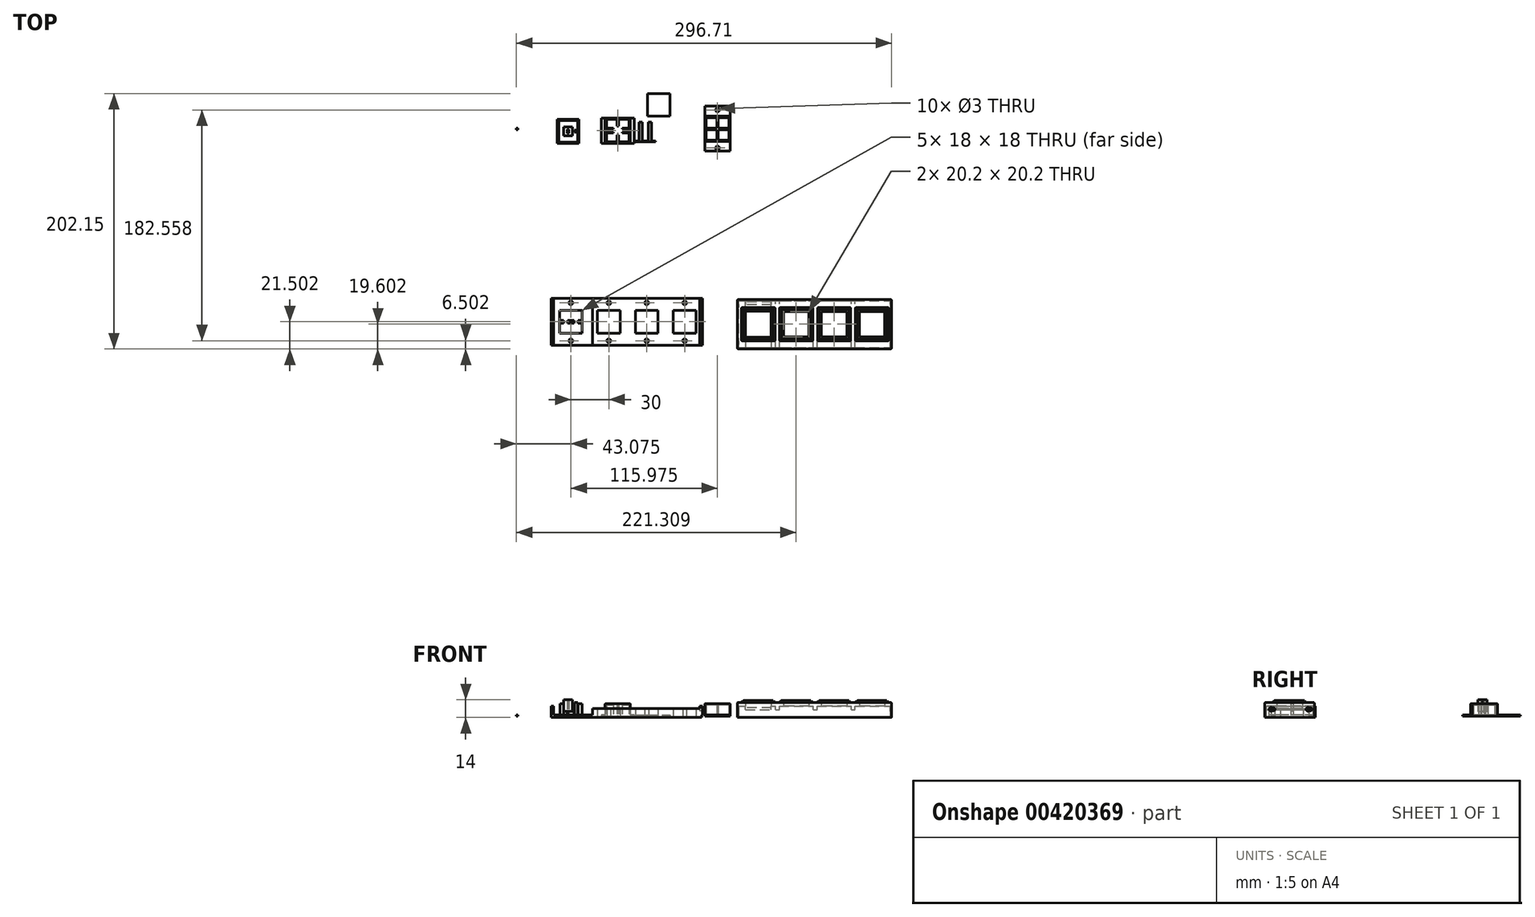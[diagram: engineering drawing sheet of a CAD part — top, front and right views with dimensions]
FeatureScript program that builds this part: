
annotation { "Feature Type Name" : "Feature", "Feature Type Description" : "" }
export const myFeature = defineFeature(function(context is Context, id is Id, definition is map)
    precondition{}
    {
        {
            var Q0;
            Q0=qCreatedBy(makeId("Top.planeOp"),FACE);
            var sketch = newSketch(context, id + "F0", { "sketchPlane" : qUnion([Q0])});
            skPoint(sketch, "E0.middle", {"position": v(0, 0) * mm});
            skLineSegment(sketch, "E1.bottom", {"start": v(10, -10) * mm, "end": v(-10, -10) * mm});
            skLineSegment(sketch, "E1.top", {"start": v(10, 10) * mm, "end": v(-10, 10) * mm});
            skLineSegment(sketch, "E1.left", {"start": v(10, -10) * mm, "end": v(10, 10) * mm});
            skLineSegment(sketch, "E1.right", {"start": v(-10, -10) * mm, "end": v(-10, 10) * mm});
            skSolve(sketch);
        }
        {
            var Q0;
            Q0=makeQuery(id+"F0.imprint","IMPRINT",FACE,{"disambiguationData":[TD([[makeQuery(id+"F0.imprint","IMPRINT",EDGE,{"derivedFrom":sQuery(id+"F0.wireOp",EDGE,"E1.bottom")}),-1.0]])]});
            extrude(context, id + "F1", {"entities" : qUnion([Q0]), "depth" : 10 * mm});
        }
        {
            var Q0;
            Q0=makeQuery(id+"F1.opExtrude","CAP_FACE",FACE,{"disambiguationData":[OSD([sQuery(id+"F0.wireOp",EDGE,"E1.bottom"),sQuery(id+"F0.wireOp",EDGE,"E1.top"),sQuery(id+"F0.wireOp",EDGE,"E1.left"),sQuery(id+"F0.wireOp",EDGE,"E1.right")])],"isStart":true});
            shell(context, id + "F2", {"entities" : qUnion([Q0]), "thickness" : 1 * mm});
        }
        {
            var Q0;
            Q0=qCreatedBy(makeId("Top.planeOp"),FACE);
            var sketch = newSketch(context, id + "F3", { "sketchPlane" : qUnion([Q0])});
            skLineSegment(sketch, "E2.bottom", {"start": v(0.5, -9) * mm, "end": v(-0.5, -9) * mm});
            skLineSegment(sketch, "E2.top", {"start": v(0.5, 9) * mm, "end": v(-0.5, 9) * mm});
            skLineSegment(sketch, "E2.left", {"start": v(0.5, -9) * mm, "end": v(0.5, -0.5) * mm});
            skLineSegment(sketch, "E2.right", {"start": v(-0.5, -9) * mm, "end": v(-0.5, -0.5) * mm});
            skLineSegment(sketch, "E3.bottom", {"start": v(9, 0.5) * mm, "end": v(0.5, 0.5) * mm});
            skLineSegment(sketch, "E3.top", {"start": v(9, -0.5) * mm, "end": v(0.5, -0.5) * mm});
            skLineSegment(sketch, "E3.left", {"start": v(9, 0.5) * mm, "end": v(9, -0.5) * mm});
            skLineSegment(sketch, "E3.right", {"start": v(-9, 0.5) * mm, "end": v(-9, -0.5) * mm});
            skLineSegment(sketch, "E4.trimOffspring", {"start": v(-0.5, 0.5) * mm, "end": v(-0.5, 9) * mm});
            skLineSegment(sketch, "E5.trimOffspring", {"start": v(-0.5, -0.5) * mm, "end": v(-9, -0.5) * mm});
            skLineSegment(sketch, "E6.trimOffspring", {"start": v(0.5, 0.5) * mm, "end": v(0.5, 9) * mm});
            skLineSegment(sketch, "E7.trimOffspring", {"start": v(-0.5, 0.5) * mm, "end": v(-9, 0.5) * mm});
            skSolve(sketch);
        }
        {
            var Q0;
            Q0=qSketchRegion(id+"F3",true);
            extrude(context, id + "F4", {"entities" : qUnion([Q0]), "operationType" : NewBodyOperationType.ADD, "depth" : 9 * mm});
        }
        {
            var Q0;
            Q0=qCreatedBy(makeId("Top.planeOp"),FACE);
            var sketch = newSketch(context, id + "F5", { "sketchPlane" : qUnion([Q0])});
            skLineSegment(sketch, "E8.bottom", {"start": v(-10, -9.5) * mm, "end": v(10, -9.5) * mm});
            skLineSegment(sketch, "E8.top", {"start": v(-10, -17.5) * mm, "end": v(10, -17.5) * mm});
            skLineSegment(sketch, "E8.left", {"start": v(-10, -9.5) * mm, "end": v(-10, -17.5) * mm});
            skLineSegment(sketch, "E8.right", {"start": v(10, -9.5) * mm, "end": v(10, -17.5) * mm});
            skLineSegment(sketch, "E9.bottom", {"start": v(-10, 10) * mm, "end": v(10, 10) * mm});
            skLineSegment(sketch, "E9.top", {"start": v(-10, 18) * mm, "end": v(10, 18) * mm});
            skLineSegment(sketch, "E9.left", {"start": v(-10, 10) * mm, "end": v(-10, 18) * mm});
            skLineSegment(sketch, "E9.right", {"start": v(10, 10) * mm, "end": v(10, 18) * mm});
            skLineSegment(sketch, "E10.bottom", {"start": v(-10, -9.5) * mm, "end": v(-13, -9.5) * mm, "construction": true});
            skLineSegment(sketch, "E10.top", {"start": v(-10, 10) * mm, "end": v(-13, 10) * mm, "construction": true});
            skLineSegment(sketch, "E10.left", {"start": v(-10, -9.5) * mm, "end": v(-10, 10) * mm});
            skLineSegment(sketch, "E10.right", {"start": v(-13, -9.5) * mm, "end": v(-13, 10) * mm, "construction": true});
            skLineSegment(sketch, "E11.bottom", {"start": v(10, -9.5) * mm, "end": v(13, -9.5) * mm, "construction": true});
            skLineSegment(sketch, "E11.top", {"start": v(10, 10) * mm, "end": v(13, 10) * mm, "construction": true});
            skLineSegment(sketch, "E11.left", {"start": v(10, -9.5) * mm, "end": v(10, 10) * mm});
            skLineSegment(sketch, "E11.right", {"start": v(13, -9.5) * mm, "end": v(13, 10) * mm, "construction": true});
            skCircle(sketch, "E12", {"center": v(0, 15) * mm, "radius": 1.5 * mm});
            skCircle(sketch, "E13", {"center": v(0, -15) * mm, "radius": 1.5 * mm});
            skSolve(sketch);
        }
        {
            var Q0;
            Q0=makeQuery(id+"F5.imprint","IMPRINT",FACE,{"disambiguationData":[TD([[makeQuery(id+"F5.imprint","IMPRINT",EDGE,{"derivedFrom":sQuery(id+"F5.wireOp",EDGE,"E10.bottom")}),-1.0]])]});
            var Q1;
            Q1=makeQuery(id+"F5.imprint","IMPRINT",FACE,{"disambiguationData":[TD([[makeQuery(id+"F5.imprint","IMPRINT",EDGE,{"derivedFrom":sQuery(id+"F5.wireOp",EDGE,"E8.bottom")}),-1.0]])]});
            var Q2;
            Q2=makeQuery(id+"F5.imprint","IMPRINT",FACE,{"disambiguationData":[TD([[makeQuery(id+"F5.imprint","IMPRINT",EDGE,{"derivedFrom":sQuery(id+"F5.wireOp",EDGE,"E11.bottom")}),1.0]])]});
            var Q3;
            Q3=makeQuery(id+"F5.imprint","IMPRINT",FACE,{"disambiguationData":[TD([[makeQuery(id+"F5.imprint","IMPRINT",EDGE,{"derivedFrom":sQuery(id+"F5.wireOp",EDGE,"E9.bottom")}),1.0]])]});
            extrude(context, id + "F6", {"entities" : qUnion([Q0, Q1, Q2, Q3]), "operationType" : NewBodyOperationType.ADD, "depth" : 1 * mm});
        }
        {
            var Q0;
            Q0=qCreatedBy(makeId("Top.planeOp"),FACE);
            var sketch = newSketch(context, id + "F7", { "sketchPlane" : qUnion([Q0])});
            skLineSegment(sketch, "E14.bottom", {"start": v(-88.88, 8.7) * mm, "end": v(-68.88, 8.7) * mm});
            skLineSegment(sketch, "E14.top", {"start": v(-88.88, -11.3) * mm, "end": v(-68.88, -11.3) * mm});
            skLineSegment(sketch, "E14.left", {"start": v(-88.88, 8.7) * mm, "end": v(-88.88, -11.3) * mm});
            skLineSegment(sketch, "E14.right", {"start": v(-68.88, 8.7) * mm, "end": v(-68.88, -11.3) * mm});
            skSolve(sketch);
        }
        {
            var Q0;
            Q0=makeQuery(id+"F7.imprint","IMPRINT",FACE,{"disambiguationData":[TD([[makeQuery(id+"F7.imprint","IMPRINT",EDGE,{"derivedFrom":sQuery(id+"F7.wireOp",EDGE,"E14.bottom")}),-1.0]])]});
            extrude(context, id + "F8", {"entities" : qUnion([Q0]), "depth" : 10 * mm});
        }
        {
            var Q0;
            Q0=makeQuery(id+"F13.boolean.opBoolean","MERGE",FACE,{"derivedFrom":[makeQuery(id+"F8.opExtrude","CAP_FACE",FACE,{"disambiguationData":[OSD([sQuery(id+"F7.wireOp",EDGE,"E14.bottom"),sQuery(id+"F7.wireOp",EDGE,"E14.top"),sQuery(id+"F7.wireOp",EDGE,"E14.left"),sQuery(id+"F7.wireOp",EDGE,"E14.right")])],"isStart":true}),makeQuery(id+"F13.opExtrude","CAP_FACE",FACE,{"disambiguationData":[OSD([sQuery(id+"F12.wireOp",EDGE,"E22.bottom"),sQuery(id+"F12.wireOp",EDGE,"E22.top"),sQuery(id+"F12.wireOp",EDGE,"E22.left"),sQuery(id+"F12.wireOp",EDGE,"E22.right"),sQuery(id+"F12.wireOp",EDGE,"E23.trimOffspring"),sQuery(id+"F12.wireOp",EDGE,"E25.trimOffspring"),sQuery(id+"F12.wireOp",EDGE,"E27"),sQuery(id+"F12.wireOp",EDGE,"E28"),sQuery(id+"F12.wireOp",EDGE,"E29.bottom"),sQuery(id+"F12.wireOp",EDGE,"E29.top"),sQuery(id+"F12.wireOp",EDGE,"E29.left"),sQuery(id+"F12.wireOp",EDGE,"E30.bottom"),sQuery(id+"F12.wireOp",EDGE,"E30.top"),sQuery(id+"F12.wireOp",EDGE,"E30.left"),sQuery(id+"F12.wireOp",EDGE,"E31.bottom"),sQuery(id+"F12.wireOp",EDGE,"E31.top"),sQuery(id+"F12.wireOp",EDGE,"E31.right"),sQuery(id+"F12.wireOp",EDGE,"E32.bottom"),sQuery(id+"F12.wireOp",EDGE,"E32.top"),sQuery(id+"F12.wireOp",EDGE,"E32.right")])],"isStart":true})]});
            var sketch = newSketch(context, id + "F9", { "sketchPlane" : qUnion([Q0])});
            skLineSegment(sketch, "E15.bottom", {"start": v(-88.88, 11.3) * mm, "end": v(-68.88, 11.3) * mm});
            skLineSegment(sketch, "E15.top", {"start": v(-88.88, 14.3) * mm, "end": v(-68.88, 14.3) * mm, "construction": true});
            skLineSegment(sketch, "E15.left", {"start": v(-88.88, 11.3) * mm, "end": v(-88.88, 14.3) * mm, "construction": true});
            skLineSegment(sketch, "E15.right", {"start": v(-68.88, 11.3) * mm, "end": v(-68.88, 14.3) * mm, "construction": true});
            skLineSegment(sketch, "E16.bottom", {"start": v(-88.88, -8.7) * mm, "end": v(-68.88, -8.7) * mm});
            skLineSegment(sketch, "E16.top", {"start": v(-88.88, -11.7) * mm, "end": v(-68.88, -11.7) * mm});
            skLineSegment(sketch, "E16.left", {"start": v(-88.88, -8.7) * mm, "end": v(-88.88, -11.7) * mm, "construction": true});
            skLineSegment(sketch, "E16.right", {"start": v(-68.88, -8.7) * mm, "end": v(-68.88, -11.7) * mm, "construction": true});
            skLineSegment(sketch, "E17.bottom", {"start": v(-88.88, -8.7) * mm, "end": v(-91.88, -8.7) * mm});
            skLineSegment(sketch, "E17.top", {"start": v(-88.88, 11.3) * mm, "end": v(-91.88, 11.3) * mm});
            skLineSegment(sketch, "E17.left", {"start": v(-88.88, -8.7) * mm, "end": v(-88.88, 11.3) * mm});
            skLineSegment(sketch, "E17.right", {"start": v(-91.88, -8.7) * mm, "end": v(-91.88, 11.3) * mm});
            skLineSegment(sketch, "E18.bottom", {"start": v(-68.88, -8.7) * mm, "end": v(-65.88, -8.7) * mm});
            skLineSegment(sketch, "E18.top", {"start": v(-68.88, 11.3) * mm, "end": v(-65.88, 11.3) * mm});
            skLineSegment(sketch, "E18.left", {"start": v(-68.88, -8.7) * mm, "end": v(-68.88, 11.3) * mm});
            skLineSegment(sketch, "E18.right", {"start": v(-65.88, -8.7) * mm, "end": v(-65.88, 11.3) * mm});
            skLineSegment(sketch, "E19.bottom", {"start": v(-88.88, -11.7) * mm, "end": v(-68.88, -11.7) * mm, "construction": true});
            skLineSegment(sketch, "E19.top", {"start": v(-88.88, -16.7) * mm, "end": v(-68.88, -16.7) * mm, "construction": true});
            skLineSegment(sketch, "E19.left", {"start": v(-88.88, -11.7) * mm, "end": v(-88.88, -16.7) * mm, "construction": true});
            skLineSegment(sketch, "E19.right", {"start": v(-68.88, -11.7) * mm, "end": v(-68.88, -16.7) * mm, "construction": true});
            skCircle(sketch, "E20", {"center": v(-78.88, -13.7) * mm, "radius": 1.5 * mm, "construction": true});
            skSolve(sketch);
        }
        {
            var Q0;
            Q0=qSketchRegion(id+"F9",true);
            extrude(context, id + "F10", {"entities" : qUnion([Q0]), "operationType" : NewBodyOperationType.ADD, "oppositeDirection" : true, "depth" : 0.95 * mm});
        }
        {
            var Q0;
            Q0=makeQuery(id+"F8.opExtrude","CAP_FACE",FACE,{"disambiguationData":[OSD([sQuery(id+"F7.wireOp",EDGE,"E14.bottom"),sQuery(id+"F7.wireOp",EDGE,"E14.top"),sQuery(id+"F7.wireOp",EDGE,"E14.left"),sQuery(id+"F7.wireOp",EDGE,"E14.right")])],"isStart":true});
            shell(context, id + "F11", {"entities" : qUnion([Q0]), "thickness" : 1 * mm});
        }
        {
            var Q0;
            Q0=qCreatedBy(makeId("Top.planeOp"),FACE);
            var sketch = newSketch(context, id + "F12", { "sketchPlane" : qUnion([Q0])});
            skLineSegment(sketch, "E21.bottom", {"start": v(-87.88, -0.1) * mm, "end": v(-79.38, -0.1) * mm, "construction": true});
            skLineSegment(sketch, "E21.top", {"start": v(-87.88, -2.5) * mm, "end": v(-79.38, -2.5) * mm, "construction": true});
            skLineSegment(sketch, "E21.left", {"start": v(-87.88, -0.1) * mm, "end": v(-87.88, -2.5) * mm, "construction": true});
            skLineSegment(sketch, "E21.right", {"start": v(-69.88, -0.1) * mm, "end": v(-69.88, -2.5) * mm, "construction": true});
            skLineSegment(sketch, "E22.bottom", {"start": v(-79.38, 7.7) * mm, "end": v(-78.38, 7.7) * mm});
            skLineSegment(sketch, "E22.top", {"start": v(-79.38, -10.3) * mm, "end": v(-78.38, -10.3) * mm});
            skLineSegment(sketch, "E22.left", {"start": v(-79.38, 7.7) * mm, "end": v(-79.38, -0.1) * mm});
            skLineSegment(sketch, "E22.right", {"start": v(-78.38, 7.7) * mm, "end": v(-78.38, -0.1) * mm});
            skLineSegment(sketch, "E23.trimOffspring", {"start": v(-79.38, -10.3) * mm, "end": v(-79.38, -2.5) * mm});
            skLineSegment(sketch, "E24.trimOffspring", {"start": v(-78.38, -0.1) * mm, "end": v(-69.88, -0.1) * mm, "construction": true});
            skLineSegment(sketch, "E25.trimOffspring", {"start": v(-78.38, -2.5) * mm, "end": v(-78.38, -10.3) * mm});
            skLineSegment(sketch, "E26.trimOffspring", {"start": v(-78.38, -2.5) * mm, "end": v(-69.88, -2.5) * mm, "construction": true});
            skLineSegment(sketch, "E27", {"start": v(-79.38, -2.5) * mm, "end": v(-79.38, -0.1) * mm});
            skLineSegment(sketch, "E28", {"start": v(-78.38, -2.5) * mm, "end": v(-78.38, -0.1) * mm});
            skLineSegment(sketch, "E29.bottom", {"start": v(-87.88, -2.5) * mm, "end": v(-79.38, -2.5) * mm});
            skLineSegment(sketch, "E29.top", {"start": v(-87.88, -3.3) * mm, "end": v(-79.38, -3.3) * mm});
            skLineSegment(sketch, "E29.left", {"start": v(-87.88, -2.5) * mm, "end": v(-87.88, -3.3) * mm});
            skLineSegment(sketch, "E29.right", {"start": v(-79.38, -2.5) * mm, "end": v(-79.38, -3.3) * mm});
            skLineSegment(sketch, "E30.bottom", {"start": v(-87.88, -0.1) * mm, "end": v(-79.38, -0.1) * mm});
            skLineSegment(sketch, "E30.top", {"start": v(-87.88, 0.7) * mm, "end": v(-79.38, 0.7) * mm});
            skLineSegment(sketch, "E30.left", {"start": v(-87.88, -0.1) * mm, "end": v(-87.88, 0.7) * mm});
            skLineSegment(sketch, "E30.right", {"start": v(-79.38, -0.1) * mm, "end": v(-79.38, 0.7) * mm});
            skLineSegment(sketch, "E31.bottom", {"start": v(-78.38, -3.3) * mm, "end": v(-69.88, -3.3) * mm});
            skLineSegment(sketch, "E31.top", {"start": v(-78.38, -2.5) * mm, "end": v(-69.88, -2.5) * mm});
            skLineSegment(sketch, "E31.left", {"start": v(-78.38, -3.3) * mm, "end": v(-78.38, -2.5) * mm});
            skLineSegment(sketch, "E31.right", {"start": v(-69.88, -3.3) * mm, "end": v(-69.88, -2.5) * mm});
            skLineSegment(sketch, "E32.bottom", {"start": v(-78.38, -0.1) * mm, "end": v(-69.88, -0.1) * mm});
            skLineSegment(sketch, "E32.top", {"start": v(-78.38, 0.7) * mm, "end": v(-69.88, 0.7) * mm});
            skLineSegment(sketch, "E32.left", {"start": v(-78.38, -0.1) * mm, "end": v(-78.38, 0.7) * mm});
            skLineSegment(sketch, "E32.right", {"start": v(-69.88, -0.1) * mm, "end": v(-69.88, 0.7) * mm});
            skSolve(sketch);
        }
        {
            var Q0;
            Q0=makeQuery(id+"F12.imprint","IMPRINT",FACE,{"disambiguationData":[TD([[makeQuery(id+"F12.imprint","IMPRINT",EDGE,{"derivedFrom":sQuery(id+"F12.wireOp",EDGE,"E22.bottom")}),-1.0]])]});
            var Q1;
            Q1=makeQuery(id+"F12.imprint","IMPRINT",FACE,{"disambiguationData":[TD([[makeQuery(id+"F12.imprint","IMPRINT",EDGE,{"derivedFrom":sQuery(id+"F12.wireOp",EDGE,"E29.bottom")}),-1.0]])]});
            var Q2;
            Q2=makeQuery(id+"F12.imprint","IMPRINT",FACE,{"disambiguationData":[TD([[makeQuery(id+"F12.imprint","IMPRINT",EDGE,{"derivedFrom":sQuery(id+"F12.wireOp",EDGE,"E30.bottom")}),1.0]])]});
            var Q3;
            Q3=makeQuery(id+"F12.imprint","IMPRINT",FACE,{"disambiguationData":[TD([[makeQuery(id+"F12.imprint","IMPRINT",EDGE,{"derivedFrom":sQuery(id+"F12.wireOp",EDGE,"E32.bottom")}),1.0]])]});
            var Q4;
            Q4=makeQuery(id+"F12.imprint","IMPRINT",FACE,{"disambiguationData":[TD([[makeQuery(id+"F12.imprint","IMPRINT",EDGE,{"derivedFrom":sQuery(id+"F12.wireOp",EDGE,"E31.bottom")}),1.0]])]});
            var Q5;
            Q5=sQuery(id+"F12.wireOp",EDGE,"E22.left");
            var Q6;
            Q6=sQuery(id+"F12.wireOp",EDGE,"E23.trimOffspring");
            var Q7;
            Q7=sQuery(id+"F12.wireOp",EDGE,"E21.top");
            var Q8;
            Q8=sQuery(id+"F12.wireOp",EDGE,"E24.trimOffspring");
            var Q9;
            Q9=sQuery(id+"F12.wireOp",EDGE,"E22.bottom");
            var Q10;
            Q10=sQuery(id+"F12.wireOp",EDGE,"E22.right");
            var Q11;
            Q11=sQuery(id+"F12.wireOp",EDGE,"E22.top");
            var Q12;
            Q12=sQuery(id+"F12.wireOp",EDGE,"E21.bottom");
            var Q13;
            Q13=sQuery(id+"F12.wireOp",EDGE,"E25.trimOffspring");
            var Q14;
            Q14=sQuery(id+"F12.wireOp",EDGE,"E26.trimOffspring");
            var Q15;
            Q15=sQuery(id+"F12.wireOp",EDGE,"E21.right");
            var Q16;
            Q16=sQuery(id+"F12.wireOp",EDGE,"E21.left");
            extrude(context, id + "F13", {"entities" : qUnion([Q0, Q1, Q2, Q3, Q4]), "operationType" : NewBodyOperationType.ADD, "surfaceEntities" : qUnion([Q5, Q6, Q7, Q8, Q9, Q10, Q11, Q12, Q13, Q14, Q15, Q16]), "depth" : 9 * mm});
        }
        {
            var Q0;
            Q0=makeQuery(id+"F13.boolean.opBoolean","MERGE",FACE,{"derivedFrom":[makeQuery(id+"F8.opExtrude","CAP_FACE",FACE,{"disambiguationData":[OSD([sQuery(id+"F7.wireOp",EDGE,"E14.bottom"),sQuery(id+"F7.wireOp",EDGE,"E14.top"),sQuery(id+"F7.wireOp",EDGE,"E14.left"),sQuery(id+"F7.wireOp",EDGE,"E14.right")])],"isStart":true}),makeQuery(id+"F13.opExtrude","CAP_FACE",FACE,{"disambiguationData":[OSD([sQuery(id+"F12.wireOp",EDGE,"E21.bottom"),sQuery(id+"F12.wireOp",EDGE,"E21.top"),sQuery(id+"F12.wireOp",EDGE,"E21.left"),sQuery(id+"F12.wireOp",EDGE,"E21.right"),sQuery(id+"F12.wireOp",EDGE,"E22.bottom"),sQuery(id+"F12.wireOp",EDGE,"E22.top"),sQuery(id+"F12.wireOp",EDGE,"E22.left"),sQuery(id+"F12.wireOp",EDGE,"E22.right"),sQuery(id+"F12.wireOp",EDGE,"E23.trimOffspring"),sQuery(id+"F12.wireOp",EDGE,"E24.trimOffspring"),sQuery(id+"F12.wireOp",EDGE,"E25.trimOffspring"),sQuery(id+"F12.wireOp",EDGE,"E26.trimOffspring")])],"isStart":true})]});
            var sketch = newSketch(context, id + "F14", { "sketchPlane" : qUnion([Q0])});
            skLineSegment(sketch, "E33.bottom", {"start": v(-75.28, -2.3) * mm, "end": v(-82.48, -2.3) * mm});
            skLineSegment(sketch, "E33.top", {"start": v(-75.28, 4.9) * mm, "end": v(-82.48, 4.9) * mm});
            skLineSegment(sketch, "E33.left", {"start": v(-75.28, -2.3) * mm, "end": v(-75.28, 4.9) * mm});
            skLineSegment(sketch, "E33.right", {"start": v(-82.48, -2.3) * mm, "end": v(-82.48, 4.9) * mm});
            skPoint(sketch, "E33.middle.positionSnap1", {"position": v(-88.88, 1.8) * mm});
            skSolve(sketch);
        }
        {
            var Q0;
            {var subQ1=makeQuery(id+"F13.opExtrude","CAP_EDGE",EDGE,{"disambiguationData":[OSD([sQuery(id+"F12.wireOp",EDGE,"E22.right")])],"isStart":true});var subQ3=sQuery(id+"F14.wireOp",EDGE,"E33.bottom");var subQ4=makeQuery(id+"F14.imprint","INTERSECT",VERTEX,{"derivedFrom":[subQ1,subQ3]});Q0=makeQuery(id+"F14.imprint","IMPRINT",FACE,{"disambiguationData":[TD([[makeQuery(id+"F14.imprint","IMPRINT",EDGE,{"disambiguationData":[TD([[subQ4,-1.0]])],"derivedFrom":subQ3}),-1.0]])]});}
            extrude(context, id + "F15", {"entities" : qUnion([Q0]), "operationType" : NewBodyOperationType.REMOVE, "oppositeDirection" : true, "depth" : 9 * mm});
        }
        {
            var Q0;
            Q0=qCreatedBy(makeId("Top.planeOp"),FACE);
            var sketch = newSketch(context, id + "F16", { "sketchPlane" : qUnion([Q0])});
            skLineSegment(sketch, "E34.bottom", {"start": v(-126.7, 7.66) * mm, "end": v(-109.7, 7.66) * mm});
            skLineSegment(sketch, "E34.top", {"start": v(-126.7, -11.34) * mm, "end": v(-109.7, -11.34) * mm});
            skLineSegment(sketch, "E34.left", {"start": v(-126.7, 7.66) * mm, "end": v(-126.7, -11.34) * mm});
            skLineSegment(sketch, "E34.right", {"start": v(-109.7, 7.66) * mm, "end": v(-109.7, -11.34) * mm});
            skLineSegment(sketch, "E35.top", {"start": v(-126.7, 15.66) * mm, "end": v(-109.7, 15.66) * mm});
            skLineSegment(sketch, "E35.left", {"start": v(-126.7, 7.66) * mm, "end": v(-126.7, 15.66) * mm});
            skLineSegment(sketch, "E35.right", {"start": v(-109.7, 7.66) * mm, "end": v(-109.7, 15.66) * mm});
            skLineSegment(sketch, "E36.top", {"start": v(-126.7, -19.34) * mm, "end": v(-109.7, -19.34) * mm});
            skLineSegment(sketch, "E36.left", {"start": v(-126.7, -11.34) * mm, "end": v(-126.7, -19.34) * mm});
            skLineSegment(sketch, "E36.right", {"start": v(-109.7, -11.34) * mm, "end": v(-109.7, -19.34) * mm});
            skLineSegment(sketch, "E37.bottom", {"start": v(-118.94, 7.66) * mm, "end": v(-117.44, 7.66) * mm, "construction": true});
            skLineSegment(sketch, "E37.top", {"start": v(-118.94, -11.34) * mm, "end": v(-117.44, -11.34) * mm, "construction": true});
            skLineSegment(sketch, "E37.left", {"start": v(-118.94, 7.66) * mm, "end": v(-118.94, -1.09) * mm, "construction": true});
            skLineSegment(sketch, "E37.right", {"start": v(-117.44, 7.66) * mm, "end": v(-117.44, -1.09) * mm, "construction": true});
            skLineSegment(sketch, "E38.bottom", {"start": v(-126.7, -1.09) * mm, "end": v(-123.07, -1.09) * mm, "construction": true});
            skLineSegment(sketch, "E38.top", {"start": v(-126.7, -2.59) * mm, "end": v(-123.07, -2.59) * mm, "construction": true});
            skLineSegment(sketch, "E38.left", {"start": v(-126.7, -1.09) * mm, "end": v(-126.7, -2.59) * mm, "construction": true});
            skLineSegment(sketch, "E38.right", {"start": v(-109.7, -1.09) * mm, "end": v(-109.7, -2.59) * mm, "construction": true});
            skLineSegment(sketch, "E39.0", {"start": v(-125.7, 6.66) * mm, "end": v(-110.7, 6.66) * mm});
            skLineSegment(sketch, "E39.1", {"start": v(-125.7, 6.66) * mm, "end": v(-125.7, -10.34) * mm});
            skLineSegment(sketch, "E39.2", {"start": v(-125.7, -10.34) * mm, "end": v(-110.7, -10.34) * mm});
            skLineSegment(sketch, "E39.3", {"start": v(-110.7, 6.66) * mm, "end": v(-110.7, -10.34) * mm});
            skCircle(sketch, "E40", {"center": v(-118.2, 13.16) * mm, "radius": 1.5 * mm});
            skPoint(sketch, "E41", {"position": v(-118.2, 7.66) * mm});
            skCircle(sketch, "E42", {"center": v(-118.2, -16.84) * mm, "radius": 1.5 * mm});
            skPoint(sketch, "E42.centerSnap0", {"position": v(-118.2, 15.66) * mm});
            skLineSegment(sketch, "E43.bottom", {"start": v(-125.3, 5.6) * mm, "end": v(-119.3, 5.6) * mm, "construction": true});
            skLineSegment(sketch, "E43.top", {"start": v(-125.3, -0.4) * mm, "end": v(-119.3, -0.4) * mm, "construction": true});
            skLineSegment(sketch, "E43.left", {"start": v(-125.3, 5.6) * mm, "end": v(-125.3, -0.4) * mm, "construction": true});
            skLineSegment(sketch, "E43.right", {"start": v(-119.3, 5.6) * mm, "end": v(-119.3, -0.4) * mm, "construction": true});
            skLineSegment(sketch, "E44.bottom", {"start": v(-101.6, 6.16) * mm, "end": v(-94.6, 6.16) * mm, "construction": true});
            skLineSegment(sketch, "E44.top", {"start": v(-101.6, -0.84) * mm, "end": v(-94.6, -0.84) * mm, "construction": true});
            skLineSegment(sketch, "E44.left", {"start": v(-101.6, 6.16) * mm, "end": v(-101.6, -0.84) * mm, "construction": true});
            skLineSegment(sketch, "E44.right", {"start": v(-94.6, 6.16) * mm, "end": v(-94.6, -0.84) * mm, "construction": true});
            skLineSegment(sketch, "E45.trimOffspring", {"start": v(-117.44, -1.09) * mm, "end": v(-114.82, -1.09) * mm, "construction": true});
            skLineSegment(sketch, "E46.trimOffspring", {"start": v(-117.44, -2.59) * mm, "end": v(-114.82, -2.59) * mm, "construction": true});
            skLineSegment(sketch, "E47.trimOffspring", {"start": v(-118.94, -2.59) * mm, "end": v(-118.94, -11.34) * mm, "construction": true});
            skLineSegment(sketch, "E48.trimOffspring", {"start": v(-117.44, -2.59) * mm, "end": v(-117.44, -11.34) * mm, "construction": true});
            skLineSegment(sketch, "E49.bottom", {"start": v(-123.07, 6.66) * mm, "end": v(-121.57, 6.66) * mm});
            skLineSegment(sketch, "E49.top", {"start": v(-123.07, -10.34) * mm, "end": v(-121.57, -10.34) * mm});
            skLineSegment(sketch, "E49.left", {"start": v(-123.07, 6.66) * mm, "end": v(-123.07, -1.09) * mm});
            skLineSegment(sketch, "E49.right", {"start": v(-121.57, 6.66) * mm, "end": v(-121.57, -1.09) * mm});
            skLineSegment(sketch, "E50.bottom", {"start": v(-114.82, 6.66) * mm, "end": v(-113.32, 6.66) * mm});
            skLineSegment(sketch, "E50.top", {"start": v(-114.82, -10.34) * mm, "end": v(-113.32, -10.34) * mm});
            skLineSegment(sketch, "E50.left", {"start": v(-114.82, 6.66) * mm, "end": v(-114.82, -1.09) * mm});
            skLineSegment(sketch, "E50.right", {"start": v(-113.32, 6.66) * mm, "end": v(-113.32, -1.09) * mm});
            skLineSegment(sketch, "E51.bottom", {"start": v(-125.7, -1.09) * mm, "end": v(-123.07, -1.09) * mm});
            skLineSegment(sketch, "E51.top", {"start": v(-125.7, -2.59) * mm, "end": v(-123.07, -2.59) * mm});
            skLineSegment(sketch, "E51.left", {"start": v(-125.7, -1.09) * mm, "end": v(-125.7, -2.59) * mm});
            skLineSegment(sketch, "E51.right", {"start": v(-110.7, -1.09) * mm, "end": v(-110.7, -2.59) * mm});
            skLineSegment(sketch, "E52.trimOffspring", {"start": v(-123.07, -2.59) * mm, "end": v(-123.07, -10.34) * mm});
            skLineSegment(sketch, "E53.trimOffspring", {"start": v(-121.57, -2.59) * mm, "end": v(-121.57, -10.34) * mm});
            skLineSegment(sketch, "E54.trimOffspring", {"start": v(-121.57, -1.09) * mm, "end": v(-118.94, -1.09) * mm, "construction": true});
            skLineSegment(sketch, "E55.trimOffspring", {"start": v(-121.57, -2.59) * mm, "end": v(-118.94, -2.59) * mm, "construction": true});
            skLineSegment(sketch, "E56.trimOffspring", {"start": v(-121.57, -1.09) * mm, "end": v(-114.82, -1.09) * mm});
            skLineSegment(sketch, "E57.trimOffspring", {"start": v(-121.57, -2.59) * mm, "end": v(-114.82, -2.59) * mm});
            skLineSegment(sketch, "E58.trimOffspring", {"start": v(-114.82, -2.59) * mm, "end": v(-114.82, -10.34) * mm});
            skLineSegment(sketch, "E59.trimOffspring", {"start": v(-113.32, -1.09) * mm, "end": v(-109.7, -1.09) * mm, "construction": true});
            skLineSegment(sketch, "E60.trimOffspring", {"start": v(-113.32, -2.59) * mm, "end": v(-113.32, -10.34) * mm});
            skLineSegment(sketch, "E61.trimOffspring", {"start": v(-113.32, -1.09) * mm, "end": v(-110.7, -1.09) * mm});
            skLineSegment(sketch, "E62.trimOffspring", {"start": v(-113.32, -2.59) * mm, "end": v(-109.7, -2.59) * mm, "construction": true});
            skLineSegment(sketch, "E63.trimOffspring", {"start": v(-113.32, -2.59) * mm, "end": v(-110.7, -2.59) * mm});
            skLineSegment(sketch, "E64.bottom", {"start": v(-117.06, 5.6) * mm, "end": v(-111.06, 5.6) * mm, "construction": true});
            skLineSegment(sketch, "E64.top", {"start": v(-117.06, -0.4) * mm, "end": v(-111.06, -0.4) * mm, "construction": true});
            skLineSegment(sketch, "E64.left", {"start": v(-117.06, 5.6) * mm, "end": v(-117.06, -0.4) * mm, "construction": true});
            skLineSegment(sketch, "E64.right", {"start": v(-111.06, 5.6) * mm, "end": v(-111.06, -0.4) * mm, "construction": true});
            skSolve(sketch);
        }
        {
            var Q0;
            Q0=makeQuery(id+"F16.imprint","IMPRINT",FACE,{"disambiguationData":[TD([[makeQuery(id+"F16.imprint","IMPRINT",EDGE,{"derivedFrom":sQuery(id+"F16.wireOp",EDGE,"E34.bottom")}),1.0]])]});
            var Q1;
            Q1=makeQuery(id+"F16.imprint","IMPRINT",FACE,{"disambiguationData":[TD([[makeQuery(id+"F16.imprint","IMPRINT",EDGE,{"derivedFrom":sQuery(id+"F16.wireOp",EDGE,"E34.top")}),-1.0]])]});
            var Q2;
            Q2=makeQuery(id+"F16.imprint","IMPRINT",FACE,{"disambiguationData":[TD([[makeQuery(id+"F16.imprint","IMPRINT",EDGE,{"derivedFrom":sQuery(id+"F16.wireOp",EDGE,"E34.left")}),1.0]])]});
            var Q3;
            Q3=makeQuery(id+"F16.imprint","IMPRINT",FACE,{"disambiguationData":[TD([[makeQuery(id+"F16.imprint","IMPRINT",EDGE,{"derivedFrom":sQuery(id+"F16.wireOp",EDGE,"0d877499-d8d4-4159-99c7-822d795fc6ca.bottom")}),-1.0]])]});
            var Q4;
            Q4=makeQuery(id+"F16.imprint","IMPRINT",FACE,{"disambiguationData":[TD([[makeQuery(id+"F16.imprint","IMPRINT",EDGE,{"derivedFrom":sQuery(id+"F16.wireOp",EDGE,"c0df8190-0039-47ec-86a2-d0705ce6734e.bottom")}),-1.0]])]});
            var Q5;
            Q5=makeQuery(id+"F16.imprint","IMPRINT",FACE,{"disambiguationData":[TD([[makeQuery(id+"F16.imprint","IMPRINT",EDGE,{"derivedFrom":sQuery(id+"F16.wireOp",EDGE,"hlkj7elJ-mpTF-eRwW-Toyz-55aFHtf3xgrz.bottom")}),-1.0]])]});
            var Q6;
            Q6=makeQuery(id+"F16.imprint","IMPRINT",FACE,{"disambiguationData":[TD([[makeQuery(id+"F16.imprint","IMPRINT",EDGE,{"derivedFrom":sQuery(id+"F16.wireOp",EDGE,"E49.bottom")}),-1.0]])]});
            var Q7;
            Q7=makeQuery(id+"F16.imprint","IMPRINT",FACE,{"disambiguationData":[TD([[makeQuery(id+"F16.imprint","IMPRINT",EDGE,{"derivedFrom":sQuery(id+"F16.wireOp",EDGE,"E50.bottom")}),-1.0]])]});
            extrude(context, id + "F17", {"entities" : qUnion([Q0, Q1, Q2, Q3, Q4, Q5, Q6, Q7]), "depth" : 1 * mm});
        }
        {
            var Q0;
            Q0=makeQuery(id+"F17.opExtrude","CAP_FACE",FACE,{"disambiguationData":[OSD([sQuery(id+"F16.wireOp",EDGE,"E34.left"),sQuery(id+"F16.wireOp",EDGE,"E34.right"),sQuery(id+"F16.wireOp",EDGE,"E35.top"),sQuery(id+"F16.wireOp",EDGE,"E35.left"),sQuery(id+"F16.wireOp",EDGE,"E35.right"),sQuery(id+"F16.wireOp",EDGE,"E36.top"),sQuery(id+"F16.wireOp",EDGE,"E36.left"),sQuery(id+"F16.wireOp",EDGE,"E36.right"),sQuery(id+"F16.wireOp",EDGE,"E39.0"),sQuery(id+"F16.wireOp",EDGE,"E39.1"),sQuery(id+"F16.wireOp",EDGE,"E39.2"),sQuery(id+"F16.wireOp",EDGE,"E39.3"),sQuery(id+"F16.wireOp",EDGE,"0d877499-d8d4-4159-99c7-822d795fc6ca.bottom"),sQuery(id+"F16.wireOp",EDGE,"0d877499-d8d4-4159-99c7-822d795fc6ca.top"),sQuery(id+"F16.wireOp",EDGE,"c0df8190-0039-47ec-86a2-d0705ce6734e.bottom"),sQuery(id+"F16.wireOp",EDGE,"c0df8190-0039-47ec-86a2-d0705ce6734e.top"),sQuery(id+"F16.wireOp",EDGE,"E40"),sQuery(id+"F16.wireOp",EDGE,"E42"),sQuery(id+"F16.wireOp",EDGE,"hlkj7elJ-mpTF-eRwW-Toyz-55aFHtf3xgrz.left"),sQuery(id+"F16.wireOp",EDGE,"hlkj7elJ-mpTF-eRwW-Toyz-55aFHtf3xgrz.right")])],"isStart":false});
            var sketch = newSketch(context, id + "F18", { "sketchPlane" : qUnion([Q0])});
            skLineSegment(sketch, "E65.bottom", {"start": v(-118.94, -0.34) * mm, "end": v(-117.44, -0.34) * mm});
            skLineSegment(sketch, "E65.top", {"start": v(-118.94, -3.34) * mm, "end": v(-117.44, -3.34) * mm});
            skLineSegment(sketch, "E65.left", {"start": v(-118.94, -0.34) * mm, "end": v(-118.94, -3.34) * mm});
            skLineSegment(sketch, "E65.right", {"start": v(-117.44, -0.34) * mm, "end": v(-117.44, -3.34) * mm});
            skSolve(sketch);
        }
        {
            var Q0;
            {var subQ0=sQuery(id+"F18.wireOp",EDGE,"E65.left");var subQ1=makeQuery(id+"F17.opExtrude","CAP_EDGE",EDGE,{"disambiguationData":[OSD([sQuery(id+"F16.wireOp",EDGE,"E56.trimOffspring")])],"isStart":false});var subQ2=makeQuery(id+"F18.imprint","INTERSECT",VERTEX,{"derivedFrom":[subQ1,subQ0]});Q0=makeQuery(id+"F18.imprint","IMPRINT",FACE,{"disambiguationData":[TD([[makeQuery(id+"F18.imprint","IMPRINT",EDGE,{"disambiguationData":[TD([[subQ2,-1.0]])],"derivedFrom":subQ0}),1.0]])]});}
            extrude(context, id + "F19", {"entities" : qUnion([Q0]), "operationType" : NewBodyOperationType.ADD, "depth" : 3 * mm});
        }
        {
            var Q0;
            Q0=makeQuery(id+"F19.opExtrude","CAP_FACE",FACE,{"disambiguationData":[OSD([sQuery(id+"F16.wireOp",EDGE,"E56.trimOffspring"),sQuery(id+"F16.wireOp",EDGE,"E57.trimOffspring"),sQuery(id+"F18.wireOp",EDGE,"E65.left"),sQuery(id+"F18.wireOp",EDGE,"E65.right")])],"isStart":false});
            var sketch = newSketch(context, id + "F20", { "sketchPlane" : qUnion([Q0])});
            skLineSegment(sketch, "E66.bottom", {"start": v(-114.7, -5.34) * mm, "end": v(-121.7, -5.34) * mm});
            skLineSegment(sketch, "E66.top", {"start": v(-114.7, 1.66) * mm, "end": v(-121.7, 1.66) * mm});
            skLineSegment(sketch, "E66.left", {"start": v(-114.7, -5.34) * mm, "end": v(-114.7, 1.66) * mm});
            skLineSegment(sketch, "E66.right", {"start": v(-121.7, -5.34) * mm, "end": v(-121.7, 1.66) * mm});
            skPoint(sketch, "E66.middle", {"position": v(-118.2, -1.84) * mm});
            skPoint(sketch, "E66.middle.positionSnap0", {"position": v(-118.2, -1.09) * mm});
            skPoint(sketch, "E66.middle.positionSnap1", {"position": v(-118.94, -1.84) * mm});
            skPoint(sketch, "E66.centerSnap0", {"position": v(-118.2, -1.09) * mm});
            skPoint(sketch, "E66.centerSnap1", {"position": v(-118.94, -1.84) * mm});
            skSolve(sketch);
        }
        {
            var Q0;
            Q0=makeQuery(id+"F20.imprint","IMPRINT",FACE,{"disambiguationData":[TD([[makeQuery(id+"F20.imprint","IMPRINT",EDGE,{"derivedFrom":sQuery(id+"F20.wireOp",EDGE,"E66.bottom")}),-1.0]])]});
            extrude(context, id + "F21", {"entities" : qUnion([Q0]), "depth" : 9 * mm});
        }
        {
            var Q0;
            Q0=qCreatedBy(makeId("Top.planeOp"),FACE);
            var sketch = newSketch(context, id + "F22", { "sketchPlane" : qUnion([Q0])});
            skLineSegment(sketch, "E67.bottom", {"start": v(-158.05, -0.5) * mm, "end": v(-159.05, -0.5) * mm});
            skLineSegment(sketch, "E67.top", {"start": v(-158.05, 0.5) * mm, "end": v(-159.05, 0.5) * mm});
            skLineSegment(sketch, "E67.left", {"start": v(-158.05, -0.5) * mm, "end": v(-158.05, 0.5) * mm});
            skLineSegment(sketch, "E67.right", {"start": v(-159.05, -0.5) * mm, "end": v(-159.05, 0.5) * mm});
            skPoint(sketch, "E67.middle", {"position": v(-158.55, 0) * mm});
            skSolve(sketch);
        }
        {
            var Q0;
            Q0=qSketchRegion(id+"F22",true);
            extrude(context, id + "F23", {"entities" : qUnion([Q0]), "depth" : 1 * mm});
        }
        {
            var Q0;
            Q0=makeQuery(id+"F17.opExtrude","CAP_FACE",FACE,{"disambiguationData":[OSD([sQuery(id+"F16.wireOp",EDGE,"E34.left"),sQuery(id+"F16.wireOp",EDGE,"E34.right"),sQuery(id+"F16.wireOp",EDGE,"E35.top"),sQuery(id+"F16.wireOp",EDGE,"E35.left"),sQuery(id+"F16.wireOp",EDGE,"E35.right"),sQuery(id+"F16.wireOp",EDGE,"E36.top"),sQuery(id+"F16.wireOp",EDGE,"E36.left"),sQuery(id+"F16.wireOp",EDGE,"E36.right"),sQuery(id+"F16.wireOp",EDGE,"E39.0"),sQuery(id+"F16.wireOp",EDGE,"E39.1"),sQuery(id+"F16.wireOp",EDGE,"E39.2"),sQuery(id+"F16.wireOp",EDGE,"E39.3"),sQuery(id+"F16.wireOp",EDGE,"E40"),sQuery(id+"F16.wireOp",EDGE,"E42"),sQuery(id+"F16.wireOp",EDGE,"E49.left"),sQuery(id+"F16.wireOp",EDGE,"E49.right"),sQuery(id+"F16.wireOp",EDGE,"E50.left"),sQuery(id+"F16.wireOp",EDGE,"E50.right"),sQuery(id+"F16.wireOp",EDGE,"E51.bottom"),sQuery(id+"F16.wireOp",EDGE,"E51.top"),sQuery(id+"F16.wireOp",EDGE,"E52.trimOffspring"),sQuery(id+"F16.wireOp",EDGE,"E53.trimOffspring"),sQuery(id+"F16.wireOp",EDGE,"E56.trimOffspring"),sQuery(id+"F16.wireOp",EDGE,"E57.trimOffspring"),sQuery(id+"F16.wireOp",EDGE,"E58.trimOffspring"),sQuery(id+"F16.wireOp",EDGE,"E60.trimOffspring"),sQuery(id+"F16.wireOp",EDGE,"E61.trimOffspring"),sQuery(id+"F16.wireOp",EDGE,"E63.trimOffspring")])],"isStart":false});
            var sketch = newSketch(context, id + "F24", { "sketchPlane" : qUnion([Q0])});
            skPoint(sketch, "E68.firstSnap0", {"position": v(-116.13, -1.09) * mm});
            skLineSegment(sketch, "E68.bottom", {"start": v(-126.7, -1.09) * mm, "end": v(-123.07, -1.09) * mm});
            skLineSegment(sketch, "E68.top", {"start": v(-126.7, -2.59) * mm, "end": v(-123.07, -2.59) * mm});
            skLineSegment(sketch, "E68.left", {"start": v(-126.7, -1.09) * mm, "end": v(-126.7, -2.59) * mm});
            skLineSegment(sketch, "E68.right", {"start": v(-123.07, -1.09) * mm, "end": v(-123.07, -2.59) * mm});
            skLineSegment(sketch, "E69.bottom", {"start": v(-113.32, -1.09) * mm, "end": v(-109.7, -1.09) * mm});
            skLineSegment(sketch, "E69.top", {"start": v(-113.32, -2.59) * mm, "end": v(-109.7, -2.59) * mm});
            skLineSegment(sketch, "E69.left", {"start": v(-113.32, -1.09) * mm, "end": v(-113.32, -2.59) * mm});
            skLineSegment(sketch, "E69.right", {"start": v(-109.7, -1.09) * mm, "end": v(-109.7, -2.59) * mm});
            skSolve(sketch);
        }
        {
            var Q0;
            {var subQ4=sQuery(id+"F24.wireOp",EDGE,"E69.left");Q0=makeQuery(id+"F24.imprint","IMPRINT",FACE,{"disambiguationData":[TD([[makeQuery(id+"F24.imprint","IMPRINT",EDGE,{"derivedFrom":subQ4}),1.0]])]});}
            var Q1;
            {var subQ4=sQuery(id+"F24.wireOp",EDGE,"E68.left");Q1=makeQuery(id+"F24.imprint","IMPRINT",FACE,{"disambiguationData":[TD([[makeQuery(id+"F24.imprint","IMPRINT",EDGE,{"derivedFrom":subQ4}),-1.0]])]});}
            extrude(context, id + "F25", {"entities" : qUnion([Q0, Q1]), "operationType" : NewBodyOperationType.ADD, "depth" : 10 * mm});
        }
        {
            var Q0;
            Q0=qCreatedBy(makeId("Top.planeOp"),FACE);
            var sketch = newSketch(context, id + "F26", { "sketchPlane" : qUnion([Q0])});
            skLineSegment(sketch, "E70.bottom", {"start": v(-65.37, 6.18) * mm, "end": v(-48.87, 6.18) * mm});
            skLineSegment(sketch, "E70.top", {"start": v(-65.37, -10.32) * mm, "end": v(-48.87, -10.32) * mm});
            skLineSegment(sketch, "E70.left", {"start": v(-65.37, 6.18) * mm, "end": v(-65.37, -10.32) * mm});
            skLineSegment(sketch, "E70.right", {"start": v(-48.87, 6.18) * mm, "end": v(-48.87, -10.32) * mm});
            skLineSegment(sketch, "E71.left", {"start": v(-61.97, 5.28) * mm, "end": v(-61.97, -9.42) * mm});
            skLineSegment(sketch, "E71.right", {"start": v(-59.47, 5.28) * mm, "end": v(-59.47, -9.42) * mm});
            skLineSegment(sketch, "E72.left", {"start": v(-54.77, 5.28) * mm, "end": v(-54.77, -9.42) * mm});
            skLineSegment(sketch, "E72.right", {"start": v(-52.27, 5.28) * mm, "end": v(-52.27, -9.42) * mm});
            skLineSegment(sketch, "E73.bottom", {"start": v(-63.47, 4.48) * mm, "end": v(-57.47, 4.48) * mm});
            skLineSegment(sketch, "E73.top", {"start": v(-63.47, -1.52) * mm, "end": v(-57.47, -1.52) * mm});
            skLineSegment(sketch, "E73.left", {"start": v(-63.47, 4.48) * mm, "end": v(-63.47, -1.52) * mm});
            skLineSegment(sketch, "E73.right", {"start": v(-57.47, 4.48) * mm, "end": v(-57.47, -1.52) * mm});
            skLineSegment(sketch, "E74.bottom", {"start": v(-56.77, 4.48) * mm, "end": v(-50.77, 4.48) * mm});
            skLineSegment(sketch, "E74.top", {"start": v(-56.77, -1.52) * mm, "end": v(-50.77, -1.52) * mm});
            skLineSegment(sketch, "E74.left", {"start": v(-56.77, 4.48) * mm, "end": v(-56.77, -1.52) * mm});
            skLineSegment(sketch, "E74.right", {"start": v(-50.77, 4.48) * mm, "end": v(-50.77, -1.52) * mm});
            skLineSegment(sketch, "E75.bottom", {"start": v(-63.47, -2.62) * mm, "end": v(-57.47, -2.62) * mm});
            skLineSegment(sketch, "E75.top", {"start": v(-63.47, -8.62) * mm, "end": v(-57.47, -8.62) * mm});
            skLineSegment(sketch, "E75.left", {"start": v(-63.47, -2.62) * mm, "end": v(-63.47, -8.62) * mm});
            skLineSegment(sketch, "E75.right", {"start": v(-57.47, -2.62) * mm, "end": v(-57.47, -8.62) * mm});
            skLineSegment(sketch, "E76.bottom", {"start": v(-56.77, -2.62) * mm, "end": v(-50.77, -2.62) * mm});
            skLineSegment(sketch, "E76.top", {"start": v(-56.77, -8.62) * mm, "end": v(-50.77, -8.62) * mm});
            skLineSegment(sketch, "E76.left", {"start": v(-56.77, -2.62) * mm, "end": v(-56.77, -8.62) * mm});
            skLineSegment(sketch, "E76.right", {"start": v(-50.77, -2.62) * mm, "end": v(-50.77, -8.62) * mm});
            skLineSegment(sketch, "E77.top", {"start": v(-65.37, 5.28) * mm, "end": v(-48.87, 5.28) * mm});
            skLineSegment(sketch, "E77.left", {"start": v(-65.37, 6.18) * mm, "end": v(-65.37, 5.28) * mm});
            skLineSegment(sketch, "E77.right", {"start": v(-48.87, 6.18) * mm, "end": v(-48.87, 5.28) * mm});
            skLineSegment(sketch, "E78.bottom", {"start": v(-65.37, -10.32) * mm, "end": v(-54.77, -10.32) * mm});
            skLineSegment(sketch, "E78.top", {"start": v(-65.37, -9.42) * mm, "end": v(-48.87, -9.42) * mm});
            skLineSegment(sketch, "E78.left", {"start": v(-65.37, -10.32) * mm, "end": v(-65.37, -9.42) * mm});
            skLineSegment(sketch, "E78.right", {"start": v(-48.87, -10.32) * mm, "end": v(-48.87, -9.42) * mm});
            skLineSegment(sketch, "E79.bottom", {"start": v(-65.37, -9.42) * mm, "end": v(-64.47, -9.42) * mm});
            skLineSegment(sketch, "E79.top", {"start": v(-65.37, 5.28) * mm, "end": v(-64.47, 5.28) * mm});
            skLineSegment(sketch, "E79.left", {"start": v(-65.37, -9.42) * mm, "end": v(-65.37, 5.28) * mm});
            skLineSegment(sketch, "E79.right", {"start": v(-64.47, -9.42) * mm, "end": v(-64.47, 5.28) * mm});
            skLineSegment(sketch, "E80.bottom", {"start": v(-48.87, 5.28) * mm, "end": v(-49.77, 5.28) * mm});
            skLineSegment(sketch, "E80.top", {"start": v(-48.87, -9.42) * mm, "end": v(-49.77, -9.42) * mm});
            skLineSegment(sketch, "E80.left", {"start": v(-48.87, 5.28) * mm, "end": v(-48.87, -9.42) * mm});
            skLineSegment(sketch, "E80.right", {"start": v(-49.77, 5.28) * mm, "end": v(-49.77, -9.42) * mm});
            skLineSegment(sketch, "E81.trimOffspring", {"start": v(-52.27, -10.32) * mm, "end": v(-48.87, -10.32) * mm});
            skSolve(sketch);
        }
        {
            var Q0;
            Q0=makeQuery(id+"F26.imprint","IMPRINT",FACE,{"disambiguationData":[TD([[makeQuery(id+"F26.imprint","IMPRINT",EDGE,{"derivedFrom":sQuery(id+"F26.wireOp",EDGE,"E70.top")}),1.0]])]});
            var Q1;
            Q1=makeQuery(id+"F26.imprint","IMPRINT",FACE,{"disambiguationData":[TD([[makeQuery(id+"F26.imprint","IMPRINT",EDGE,{"derivedFrom":sQuery(id+"F26.wireOp",EDGE,"E79.bottom")}),1.0]])]});
            var Q2;
            Q2=makeQuery(id+"F26.imprint","IMPRINT",FACE,{"disambiguationData":[TD([[makeQuery(id+"F26.imprint","IMPRINT",EDGE,{"derivedFrom":sQuery(id+"F26.wireOp",EDGE,"E70.bottom")}),-1.0]])]});
            var Q3;
            Q3=makeQuery(id+"F26.imprint","IMPRINT",FACE,{"disambiguationData":[TD([[makeQuery(id+"F26.imprint","IMPRINT",EDGE,{"derivedFrom":sQuery(id+"F26.wireOp",EDGE,"E80.bottom")}),1.0]])]});
            var Q4;
            {var subQ0=sQuery(id+"F26.wireOp",EDGE,"E72.left");Q4=makeQuery(id+"F26.imprint","IMPRINT",FACE,{"disambiguationData":[TD([[makeQuery(id+"F26.imprint","IMPRINT",EDGE,{"derivedFrom":subQ0}),1.0]])]});}
            var Q5;
            {var subQ0=sQuery(id+"F26.wireOp",EDGE,"E71.left");Q5=makeQuery(id+"F26.imprint","IMPRINT",FACE,{"disambiguationData":[TD([[makeQuery(id+"F26.imprint","IMPRINT",EDGE,{"derivedFrom":subQ0}),1.0]])]});}
            extrude(context, id + "F27", {"entities" : qUnion([Q0, Q1, Q2, Q3, Q4, Q5]), "depth" : 1 * mm});
        }
        {
            var Q0;
            Q0=qCreatedBy(makeId("Top.planeOp"),FACE);
            var sketch = newSketch(context, id + "F28", { "sketchPlane" : qUnion([Q0])});
            skLineSegment(sketch, "E82.bottom", {"start": v(-124.98, -143.56) * mm, "end": v(-106.98, -143.56) * mm});
            skLineSegment(sketch, "E82.top", {"start": v(-124.98, -161.56) * mm, "end": v(-106.98, -161.56) * mm});
            skLineSegment(sketch, "E82.left", {"start": v(-124.98, -143.56) * mm, "end": v(-124.98, -161.56) * mm});
            skLineSegment(sketch, "E82.right", {"start": v(-106.98, -143.56) * mm, "end": v(-106.98, -161.56) * mm});
            skLineSegment(sketch, "E83.bottom", {"start": v(-116.73, -143.56) * mm, "end": v(-115.23, -143.56) * mm, "construction": true});
            skLineSegment(sketch, "E83.top", {"start": v(-116.73, -161.56) * mm, "end": v(-115.23, -161.56) * mm, "construction": true});
            skLineSegment(sketch, "E83.left", {"start": v(-116.73, -143.56) * mm, "end": v(-116.73, -151.56) * mm, "construction": true});
            skLineSegment(sketch, "E83.right", {"start": v(-115.23, -143.56) * mm, "end": v(-115.23, -151.56) * mm, "construction": true});
            skCircle(sketch, "E84", {"center": v(-115.98, -137.56) * mm, "radius": 1.5 * mm});
            skPoint(sketch, "E85", {"position": v(-115.98, -143.56) * mm});
            skCircle(sketch, "E86", {"center": v(-115.98, -167.56) * mm, "radius": 1.5 * mm});
            skLineSegment(sketch, "E87.trimOffspring", {"start": v(-115.23, -151.56) * mm, "end": v(-112.23, -151.56) * mm, "construction": true});
            skLineSegment(sketch, "E88.trimOffspring", {"start": v(-115.23, -153.56) * mm, "end": v(-112.23, -153.56) * mm, "construction": true});
            skLineSegment(sketch, "E89.trimOffspring", {"start": v(-116.73, -153.56) * mm, "end": v(-116.73, -161.56) * mm, "construction": true});
            skLineSegment(sketch, "E90.trimOffspring", {"start": v(-115.23, -153.56) * mm, "end": v(-115.23, -161.56) * mm, "construction": true});
            skLineSegment(sketch, "E91.bottom", {"start": v(-121.73, -143.56) * mm, "end": v(-119.73, -143.56) * mm});
            skLineSegment(sketch, "E91.top", {"start": v(-121.73, -161.56) * mm, "end": v(-119.73, -161.56) * mm});
            skLineSegment(sketch, "E91.left", {"start": v(-121.73, -143.56) * mm, "end": v(-121.73, -151.56) * mm});
            skLineSegment(sketch, "E91.right", {"start": v(-119.73, -143.56) * mm, "end": v(-119.73, -151.56) * mm});
            skLineSegment(sketch, "E92.bottom", {"start": v(-112.23, -143.56) * mm, "end": v(-110.23, -143.56) * mm});
            skLineSegment(sketch, "E92.top", {"start": v(-112.23, -161.56) * mm, "end": v(-110.23, -161.56) * mm});
            skLineSegment(sketch, "E92.left", {"start": v(-112.23, -143.56) * mm, "end": v(-112.23, -151.56) * mm});
            skLineSegment(sketch, "E92.right", {"start": v(-110.23, -143.56) * mm, "end": v(-110.23, -151.56) * mm});
            skLineSegment(sketch, "E93.bottom", {"start": v(-124.98, -151.56) * mm, "end": v(-121.73, -151.56) * mm});
            skLineSegment(sketch, "E93.top", {"start": v(-124.98, -153.56) * mm, "end": v(-121.73, -153.56) * mm});
            skLineSegment(sketch, "E93.left", {"start": v(-124.98, -151.56) * mm, "end": v(-124.98, -153.56) * mm});
            skLineSegment(sketch, "E93.right", {"start": v(-106.98, -151.56) * mm, "end": v(-106.98, -153.56) * mm});
            skLineSegment(sketch, "E94.trimOffspring", {"start": v(-121.73, -153.56) * mm, "end": v(-121.73, -161.56) * mm});
            skLineSegment(sketch, "E95.trimOffspring", {"start": v(-119.73, -153.56) * mm, "end": v(-119.73, -161.56) * mm});
            skLineSegment(sketch, "E96.trimOffspring", {"start": v(-119.73, -151.56) * mm, "end": v(-116.73, -151.56) * mm, "construction": true});
            skLineSegment(sketch, "E97.trimOffspring", {"start": v(-119.73, -153.56) * mm, "end": v(-116.73, -153.56) * mm, "construction": true});
            skLineSegment(sketch, "E98.trimOffspring", {"start": v(-119.73, -151.56) * mm, "end": v(-112.23, -151.56) * mm});
            skLineSegment(sketch, "E99.trimOffspring", {"start": v(-119.73, -153.56) * mm, "end": v(-112.23, -153.56) * mm});
            skLineSegment(sketch, "E100.trimOffspring", {"start": v(-112.23, -153.56) * mm, "end": v(-112.23, -161.56) * mm});
            skLineSegment(sketch, "E101.trimOffspring", {"start": v(-110.23, -153.56) * mm, "end": v(-110.23, -161.56) * mm});
            skLineSegment(sketch, "E102.trimOffspring", {"start": v(-110.23, -151.56) * mm, "end": v(-106.98, -151.56) * mm});
            skLineSegment(sketch, "E103.trimOffspring", {"start": v(-110.23, -153.56) * mm, "end": v(-106.98, -153.56) * mm});
            skLineSegment(sketch, "E104.bottom", {"start": v(-94.98, -143.56) * mm, "end": v(-76.98, -143.56) * mm});
            skLineSegment(sketch, "E104.top", {"start": v(-94.98, -161.56) * mm, "end": v(-76.98, -161.56) * mm});
            skLineSegment(sketch, "E104.left", {"start": v(-94.98, -143.56) * mm, "end": v(-94.98, -161.56) * mm});
            skLineSegment(sketch, "E104.right", {"start": v(-76.98, -143.56) * mm, "end": v(-76.98, -161.56) * mm});
            skLineSegment(sketch, "E105.bottom", {"start": v(-86.73, -143.56) * mm, "end": v(-85.23, -143.56) * mm, "construction": true});
            skLineSegment(sketch, "E105.top", {"start": v(-86.73, -161.56) * mm, "end": v(-85.23, -161.56) * mm, "construction": true});
            skLineSegment(sketch, "E105.left", {"start": v(-86.73, -143.56) * mm, "end": v(-86.73, -151.56) * mm, "construction": true});
            skLineSegment(sketch, "E105.right", {"start": v(-85.23, -143.56) * mm, "end": v(-85.23, -151.56) * mm, "construction": true});
            skLineSegment(sketch, "E106.bottom", {"start": v(-94.98, -151.56) * mm, "end": v(-91.73, -151.56) * mm, "construction": true});
            skLineSegment(sketch, "E106.top", {"start": v(-94.98, -153.56) * mm, "end": v(-91.73, -153.56) * mm, "construction": true});
            skLineSegment(sketch, "E106.left", {"start": v(-94.98, -151.56) * mm, "end": v(-94.98, -153.56) * mm, "construction": true});
            skLineSegment(sketch, "E106.right", {"start": v(-76.98, -151.56) * mm, "end": v(-76.98, -153.56) * mm, "construction": true});
            skCircle(sketch, "E107", {"center": v(-85.98, -137.56) * mm, "radius": 1.5 * mm});
            skPoint(sketch, "E108", {"position": v(-85.98, -143.56) * mm});
            skCircle(sketch, "E109", {"center": v(-85.98, -167.56) * mm, "radius": 1.5 * mm});
            skLineSegment(sketch, "E110.trimOffspring", {"start": v(-85.23, -151.56) * mm, "end": v(-82.23, -151.56) * mm, "construction": true});
            skLineSegment(sketch, "E111.trimOffspring", {"start": v(-85.23, -153.56) * mm, "end": v(-82.23, -153.56) * mm, "construction": true});
            skLineSegment(sketch, "E112.trimOffspring", {"start": v(-86.73, -153.56) * mm, "end": v(-86.73, -161.56) * mm, "construction": true});
            skLineSegment(sketch, "E113.trimOffspring", {"start": v(-85.23, -153.56) * mm, "end": v(-85.23, -161.56) * mm, "construction": true});
            skLineSegment(sketch, "E114.bottom", {"start": v(-91.73, -143.56) * mm, "end": v(-89.73, -143.56) * mm});
            skLineSegment(sketch, "E114.top", {"start": v(-91.73, -161.56) * mm, "end": v(-89.73, -161.56) * mm});
            skLineSegment(sketch, "E114.left", {"start": v(-91.73, -143.56) * mm, "end": v(-91.73, -151.56) * mm});
            skLineSegment(sketch, "E114.right", {"start": v(-89.73, -143.56) * mm, "end": v(-89.73, -151.56) * mm});
            skLineSegment(sketch, "E115.bottom", {"start": v(-82.23, -143.56) * mm, "end": v(-80.23, -143.56) * mm});
            skLineSegment(sketch, "E115.top", {"start": v(-82.23, -161.56) * mm, "end": v(-80.23, -161.56) * mm});
            skLineSegment(sketch, "E115.left", {"start": v(-82.23, -143.56) * mm, "end": v(-82.23, -151.56) * mm});
            skLineSegment(sketch, "E115.right", {"start": v(-80.23, -143.56) * mm, "end": v(-80.23, -151.56) * mm});
            skLineSegment(sketch, "E116.bottom", {"start": v(-94.98, -151.56) * mm, "end": v(-91.73, -151.56) * mm});
            skLineSegment(sketch, "E116.top", {"start": v(-94.98, -153.56) * mm, "end": v(-91.73, -153.56) * mm});
            skLineSegment(sketch, "E116.left", {"start": v(-94.98, -151.56) * mm, "end": v(-94.98, -153.56) * mm});
            skLineSegment(sketch, "E116.right", {"start": v(-76.98, -151.56) * mm, "end": v(-76.98, -153.56) * mm});
            skLineSegment(sketch, "E117.trimOffspring", {"start": v(-91.73, -153.56) * mm, "end": v(-91.73, -161.56) * mm});
            skLineSegment(sketch, "E118.trimOffspring", {"start": v(-89.73, -153.56) * mm, "end": v(-89.73, -161.56) * mm});
            skLineSegment(sketch, "E119.trimOffspring", {"start": v(-89.73, -151.56) * mm, "end": v(-86.73, -151.56) * mm, "construction": true});
            skLineSegment(sketch, "E120.trimOffspring", {"start": v(-89.73, -153.56) * mm, "end": v(-86.73, -153.56) * mm, "construction": true});
            skLineSegment(sketch, "E121.trimOffspring", {"start": v(-89.73, -151.56) * mm, "end": v(-82.23, -151.56) * mm});
            skLineSegment(sketch, "E122.trimOffspring", {"start": v(-89.73, -153.56) * mm, "end": v(-82.23, -153.56) * mm});
            skLineSegment(sketch, "E123.trimOffspring", {"start": v(-82.23, -153.56) * mm, "end": v(-82.23, -161.56) * mm});
            skLineSegment(sketch, "E124.trimOffspring", {"start": v(-80.23, -151.56) * mm, "end": v(-76.98, -151.56) * mm, "construction": true});
            skLineSegment(sketch, "E125.trimOffspring", {"start": v(-80.23, -153.56) * mm, "end": v(-80.23, -161.56) * mm});
            skLineSegment(sketch, "E126.trimOffspring", {"start": v(-80.23, -151.56) * mm, "end": v(-76.98, -151.56) * mm});
            skLineSegment(sketch, "E127.trimOffspring", {"start": v(-80.23, -153.56) * mm, "end": v(-76.98, -153.56) * mm, "construction": true});
            skLineSegment(sketch, "E128.trimOffspring", {"start": v(-80.23, -153.56) * mm, "end": v(-76.98, -153.56) * mm});
            skLineSegment(sketch, "E129.bottom", {"start": v(-64.98, -143.56) * mm, "end": v(-46.98, -143.56) * mm});
            skLineSegment(sketch, "E129.top", {"start": v(-64.98, -161.56) * mm, "end": v(-46.98, -161.56) * mm});
            skLineSegment(sketch, "E129.left", {"start": v(-64.98, -143.56) * mm, "end": v(-64.98, -161.56) * mm});
            skLineSegment(sketch, "E129.right", {"start": v(-46.98, -143.56) * mm, "end": v(-46.98, -161.56) * mm});
            skLineSegment(sketch, "E130.bottom", {"start": v(-64.98, -161.56) * mm, "end": v(-47.98, -161.56) * mm});
            skLineSegment(sketch, "E131.bottom", {"start": v(-56.73, -143.56) * mm, "end": v(-55.23, -143.56) * mm, "construction": true});
            skLineSegment(sketch, "E131.top", {"start": v(-56.73, -161.56) * mm, "end": v(-55.23, -161.56) * mm, "construction": true});
            skLineSegment(sketch, "E131.left", {"start": v(-56.73, -143.56) * mm, "end": v(-56.73, -151.56) * mm, "construction": true});
            skLineSegment(sketch, "E131.right", {"start": v(-55.23, -143.56) * mm, "end": v(-55.23, -151.56) * mm, "construction": true});
            skLineSegment(sketch, "E132.bottom", {"start": v(-64.98, -151.56) * mm, "end": v(-61.73, -151.56) * mm, "construction": true});
            skLineSegment(sketch, "E132.top", {"start": v(-64.98, -153.56) * mm, "end": v(-61.73, -153.56) * mm, "construction": true});
            skLineSegment(sketch, "E132.left", {"start": v(-64.98, -151.56) * mm, "end": v(-64.98, -153.56) * mm, "construction": true});
            skLineSegment(sketch, "E132.right", {"start": v(-46.98, -151.56) * mm, "end": v(-46.98, -153.56) * mm, "construction": true});
            skCircle(sketch, "E133", {"center": v(-55.98, -137.56) * mm, "radius": 1.5 * mm});
            skPoint(sketch, "E134", {"position": v(-55.98, -143.56) * mm});
            skCircle(sketch, "E135", {"center": v(-55.98, -167.56) * mm, "radius": 1.5 * mm});
            skLineSegment(sketch, "E136.trimOffspring", {"start": v(-55.23, -151.56) * mm, "end": v(-52.23, -151.56) * mm, "construction": true});
            skLineSegment(sketch, "E137.trimOffspring", {"start": v(-55.23, -153.56) * mm, "end": v(-52.23, -153.56) * mm, "construction": true});
            skLineSegment(sketch, "E138.trimOffspring", {"start": v(-56.73, -153.56) * mm, "end": v(-56.73, -161.56) * mm, "construction": true});
            skLineSegment(sketch, "E139.trimOffspring", {"start": v(-55.23, -153.56) * mm, "end": v(-55.23, -161.56) * mm, "construction": true});
            skLineSegment(sketch, "E140.bottom", {"start": v(-61.73, -143.56) * mm, "end": v(-59.73, -143.56) * mm});
            skLineSegment(sketch, "E140.top", {"start": v(-61.73, -161.56) * mm, "end": v(-59.73, -161.56) * mm});
            skLineSegment(sketch, "E140.left", {"start": v(-61.73, -143.56) * mm, "end": v(-61.73, -151.56) * mm});
            skLineSegment(sketch, "E140.right", {"start": v(-59.73, -143.56) * mm, "end": v(-59.73, -151.56) * mm});
            skLineSegment(sketch, "E141.bottom", {"start": v(-52.23, -143.56) * mm, "end": v(-50.23, -143.56) * mm});
            skLineSegment(sketch, "E141.top", {"start": v(-52.23, -161.56) * mm, "end": v(-50.23, -161.56) * mm});
            skLineSegment(sketch, "E141.left", {"start": v(-52.23, -143.56) * mm, "end": v(-52.23, -151.56) * mm});
            skLineSegment(sketch, "E141.right", {"start": v(-50.23, -143.56) * mm, "end": v(-50.23, -151.56) * mm});
            skLineSegment(sketch, "E142.bottom", {"start": v(-64.98, -151.56) * mm, "end": v(-61.73, -151.56) * mm});
            skLineSegment(sketch, "E142.top", {"start": v(-64.98, -153.56) * mm, "end": v(-61.73, -153.56) * mm});
            skLineSegment(sketch, "E142.left", {"start": v(-64.98, -151.56) * mm, "end": v(-64.98, -153.56) * mm});
            skLineSegment(sketch, "E142.right", {"start": v(-46.98, -151.56) * mm, "end": v(-46.98, -153.56) * mm});
            skLineSegment(sketch, "E143.trimOffspring", {"start": v(-61.73, -153.56) * mm, "end": v(-61.73, -161.56) * mm});
            skLineSegment(sketch, "E144.trimOffspring", {"start": v(-59.73, -153.56) * mm, "end": v(-59.73, -161.56) * mm});
            skLineSegment(sketch, "E145.trimOffspring", {"start": v(-59.73, -151.56) * mm, "end": v(-56.73, -151.56) * mm, "construction": true});
            skLineSegment(sketch, "E146.trimOffspring", {"start": v(-59.73, -153.56) * mm, "end": v(-56.73, -153.56) * mm, "construction": true});
            skLineSegment(sketch, "E147.trimOffspring", {"start": v(-59.73, -151.56) * mm, "end": v(-52.23, -151.56) * mm});
            skLineSegment(sketch, "E148.trimOffspring", {"start": v(-59.73, -153.56) * mm, "end": v(-52.23, -153.56) * mm});
            skLineSegment(sketch, "E149.trimOffspring", {"start": v(-52.23, -153.56) * mm, "end": v(-52.23, -161.56) * mm});
            skLineSegment(sketch, "E150.trimOffspring", {"start": v(-50.23, -151.56) * mm, "end": v(-46.98, -151.56) * mm, "construction": true});
            skLineSegment(sketch, "E151.trimOffspring", {"start": v(-50.23, -153.56) * mm, "end": v(-50.23, -161.56) * mm});
            skLineSegment(sketch, "E152.trimOffspring", {"start": v(-50.23, -151.56) * mm, "end": v(-46.98, -151.56) * mm});
            skLineSegment(sketch, "E153.trimOffspring", {"start": v(-50.23, -153.56) * mm, "end": v(-46.98, -153.56) * mm, "construction": true});
            skLineSegment(sketch, "E154.trimOffspring", {"start": v(-50.23, -153.56) * mm, "end": v(-46.98, -153.56) * mm});
            skLineSegment(sketch, "E155.bottom", {"start": v(-34.98, -143.56) * mm, "end": v(-16.98, -143.56) * mm});
            skLineSegment(sketch, "E155.top", {"start": v(-34.98, -161.56) * mm, "end": v(-16.98, -161.56) * mm});
            skLineSegment(sketch, "E155.left", {"start": v(-34.98, -143.56) * mm, "end": v(-34.98, -161.56) * mm});
            skLineSegment(sketch, "E155.right", {"start": v(-16.98, -143.56) * mm, "end": v(-16.98, -161.56) * mm});
            skLineSegment(sketch, "E156.bottom", {"start": v(-34.98, -161.56) * mm, "end": v(-17.98, -161.56) * mm});
            skLineSegment(sketch, "E157.bottom", {"start": v(-26.73, -143.56) * mm, "end": v(-25.23, -143.56) * mm, "construction": true});
            skLineSegment(sketch, "E157.top", {"start": v(-26.73, -161.56) * mm, "end": v(-25.23, -161.56) * mm, "construction": true});
            skLineSegment(sketch, "E157.left", {"start": v(-26.73, -143.56) * mm, "end": v(-26.73, -151.56) * mm, "construction": true});
            skLineSegment(sketch, "E157.right", {"start": v(-25.23, -143.56) * mm, "end": v(-25.23, -151.56) * mm, "construction": true});
            skLineSegment(sketch, "E158.bottom", {"start": v(-34.98, -151.56) * mm, "end": v(-31.73, -151.56) * mm, "construction": true});
            skLineSegment(sketch, "E158.top", {"start": v(-34.98, -153.56) * mm, "end": v(-31.73, -153.56) * mm, "construction": true});
            skLineSegment(sketch, "E158.left", {"start": v(-34.98, -151.56) * mm, "end": v(-34.98, -153.56) * mm, "construction": true});
            skLineSegment(sketch, "E158.right", {"start": v(-16.98, -151.56) * mm, "end": v(-16.98, -153.56) * mm, "construction": true});
            skCircle(sketch, "E159", {"center": v(-25.98, -137.56) * mm, "radius": 1.5 * mm});
            skPoint(sketch, "E160", {"position": v(-25.98, -143.56) * mm});
            skCircle(sketch, "E161", {"center": v(-25.98, -167.56) * mm, "radius": 1.5 * mm});
            skLineSegment(sketch, "E162.trimOffspring", {"start": v(-25.23, -151.56) * mm, "end": v(-22.23, -151.56) * mm, "construction": true});
            skLineSegment(sketch, "E163.trimOffspring", {"start": v(-25.23, -153.56) * mm, "end": v(-22.23, -153.56) * mm, "construction": true});
            skLineSegment(sketch, "E164.trimOffspring", {"start": v(-26.73, -153.56) * mm, "end": v(-26.73, -161.56) * mm, "construction": true});
            skLineSegment(sketch, "E165.trimOffspring", {"start": v(-25.23, -153.56) * mm, "end": v(-25.23, -161.56) * mm, "construction": true});
            skLineSegment(sketch, "E166.bottom", {"start": v(-31.73, -143.56) * mm, "end": v(-29.73, -143.56) * mm});
            skLineSegment(sketch, "E166.top", {"start": v(-31.73, -161.56) * mm, "end": v(-29.73, -161.56) * mm});
            skLineSegment(sketch, "E166.left", {"start": v(-31.73, -143.56) * mm, "end": v(-31.73, -151.56) * mm});
            skLineSegment(sketch, "E166.right", {"start": v(-29.73, -143.56) * mm, "end": v(-29.73, -151.56) * mm});
            skLineSegment(sketch, "E167.bottom", {"start": v(-22.23, -143.56) * mm, "end": v(-20.23, -143.56) * mm});
            skLineSegment(sketch, "E167.top", {"start": v(-22.23, -161.56) * mm, "end": v(-20.23, -161.56) * mm});
            skLineSegment(sketch, "E167.left", {"start": v(-22.23, -143.56) * mm, "end": v(-22.23, -151.56) * mm});
            skLineSegment(sketch, "E167.right", {"start": v(-20.23, -143.56) * mm, "end": v(-20.23, -151.56) * mm});
            skLineSegment(sketch, "E168.bottom", {"start": v(-34.98, -151.56) * mm, "end": v(-31.73, -151.56) * mm});
            skLineSegment(sketch, "E168.top", {"start": v(-34.98, -153.56) * mm, "end": v(-31.73, -153.56) * mm});
            skLineSegment(sketch, "E168.left", {"start": v(-34.98, -151.56) * mm, "end": v(-34.98, -153.56) * mm});
            skLineSegment(sketch, "E168.right", {"start": v(-16.98, -151.56) * mm, "end": v(-16.98, -153.56) * mm});
            skLineSegment(sketch, "E169.trimOffspring", {"start": v(-31.73, -153.56) * mm, "end": v(-31.73, -161.56) * mm});
            skLineSegment(sketch, "E170.trimOffspring", {"start": v(-29.73, -153.56) * mm, "end": v(-29.73, -161.56) * mm});
            skLineSegment(sketch, "E171.trimOffspring", {"start": v(-29.73, -151.56) * mm, "end": v(-26.73, -151.56) * mm, "construction": true});
            skLineSegment(sketch, "E172.trimOffspring", {"start": v(-29.73, -153.56) * mm, "end": v(-26.73, -153.56) * mm, "construction": true});
            skLineSegment(sketch, "E173.trimOffspring", {"start": v(-29.73, -151.56) * mm, "end": v(-22.23, -151.56) * mm});
            skLineSegment(sketch, "E174.trimOffspring", {"start": v(-29.73, -153.56) * mm, "end": v(-22.23, -153.56) * mm});
            skLineSegment(sketch, "E175.trimOffspring", {"start": v(-22.23, -153.56) * mm, "end": v(-22.23, -161.56) * mm});
            skLineSegment(sketch, "E176.trimOffspring", {"start": v(-20.23, -151.56) * mm, "end": v(-16.98, -151.56) * mm, "construction": true});
            skLineSegment(sketch, "E177.trimOffspring", {"start": v(-20.23, -153.56) * mm, "end": v(-20.23, -161.56) * mm});
            skLineSegment(sketch, "E178.trimOffspring", {"start": v(-20.23, -151.56) * mm, "end": v(-16.98, -151.56) * mm});
            skLineSegment(sketch, "E179.trimOffspring", {"start": v(-20.23, -153.56) * mm, "end": v(-16.98, -153.56) * mm, "construction": true});
            skLineSegment(sketch, "E180.trimOffspring", {"start": v(-20.23, -153.56) * mm, "end": v(-16.98, -153.56) * mm});
            skLineSegment(sketch, "E181.bottom", {"start": v(-129.58, -134.06) * mm, "end": v(-12.58, -134.06) * mm});
            skLineSegment(sketch, "E181.top", {"start": v(-129.58, -171.06) * mm, "end": v(-12.58, -171.06) * mm});
            skLineSegment(sketch, "E181.left", {"start": v(-129.58, -134.06) * mm, "end": v(-129.58, -171.06) * mm});
            skLineSegment(sketch, "E181.right", {"start": v(-12.58, -134.06) * mm, "end": v(-12.58, -171.06) * mm});
            skSolve(sketch);
        }
        {
            var Q0;
            Q0=makeQuery(id+"F28.imprint","IMPRINT",FACE,{"disambiguationData":[TD([[makeQuery(id+"F28.imprint","IMPRINT",EDGE,{"derivedFrom":sQuery(id+"F28.wireOp",EDGE,"E84")}),-1.0]])]});
            var Q1;
            Q1=makeQuery(id+"F28.imprint","IMPRINT",FACE,{"disambiguationData":[TD([[makeQuery(id+"F28.imprint","IMPRINT",EDGE,{"derivedFrom":sQuery(id+"F28.wireOp",EDGE,"E91.bottom")}),-1.0]])]});
            var Q2;
            Q2=makeQuery(id+"F28.imprint","IMPRINT",FACE,{"disambiguationData":[TD([[makeQuery(id+"F28.imprint","IMPRINT",EDGE,{"derivedFrom":sQuery(id+"F28.wireOp",EDGE,"E114.bottom")}),-1.0]])]});
            var Q3;
            Q3=makeQuery(id+"F28.imprint","IMPRINT",FACE,{"disambiguationData":[TD([[makeQuery(id+"F28.imprint","IMPRINT",EDGE,{"derivedFrom":sQuery(id+"F28.wireOp",EDGE,"E140.bottom")}),-1.0]])]});
            var Q4;
            Q4=makeQuery(id+"F28.imprint","IMPRINT",FACE,{"disambiguationData":[TD([[makeQuery(id+"F28.imprint","IMPRINT",EDGE,{"derivedFrom":sQuery(id+"F28.wireOp",EDGE,"E166.bottom")}),-1.0]])]});
            extrude(context, id + "F29", {"entities" : qUnion([Q0, Q1, Q2, Q3, Q4]), "depth" : 1 * mm});
        }
        {
            var Q0;
            Q0=qCreatedBy(makeId("Top.planeOp"),FACE);
            var sketch = newSketch(context, id + "F30", { "sketchPlane" : qUnion([Q0])});
            skLineSegment(sketch, "E182.bottom", {"start": v(15.66, -134.86) * mm, "end": v(137.66, -134.86) * mm});
            skLineSegment(sketch, "E182.top", {"start": v(15.66, -174.06) * mm, "end": v(137.66, -174.06) * mm});
            skLineSegment(sketch, "E182.left", {"start": v(15.66, -134.86) * mm, "end": v(15.66, -174.06) * mm});
            skLineSegment(sketch, "E182.right", {"start": v(137.66, -134.86) * mm, "end": v(137.66, -174.06) * mm});
            skLineSegment(sketch, "E183.bottom", {"start": v(22.06, -144.26) * mm, "end": v(42.46, -144.26) * mm});
            skLineSegment(sketch, "E183.top", {"start": v(22.06, -164.66) * mm, "end": v(42.46, -164.66) * mm});
            skLineSegment(sketch, "E183.left", {"start": v(22.06, -144.26) * mm, "end": v(22.06, -164.66) * mm});
            skLineSegment(sketch, "E183.right", {"start": v(42.46, -144.26) * mm, "end": v(42.46, -164.66) * mm});
            skCircle(sketch, "E184", {"center": v(31.96, -139.46) * mm, "radius": 1.5 * mm, "construction": true});
            skCircle(sketch, "E185", {"center": v(31.96, -169.46) * mm, "radius": 1.5 * mm, "construction": true});
            skLineSegment(sketch, "E186.bottom", {"start": v(52.16, -144.36) * mm, "end": v(72.36, -144.36) * mm});
            skLineSegment(sketch, "E186.top", {"start": v(52.16, -164.56) * mm, "end": v(72.36, -164.56) * mm});
            skLineSegment(sketch, "E186.left", {"start": v(52.16, -144.36) * mm, "end": v(52.16, -164.56) * mm});
            skLineSegment(sketch, "E186.right", {"start": v(72.36, -144.36) * mm, "end": v(72.36, -164.56) * mm});
            skCircle(sketch, "E187", {"center": v(62.26, -139.46) * mm, "radius": 1.5 * mm, "construction": true});
            skCircle(sketch, "E188", {"center": v(62.26, -169.46) * mm, "radius": 1.5 * mm, "construction": true});
            skLineSegment(sketch, "E189.bottom", {"start": v(82.16, -144.36) * mm, "end": v(102.36, -144.36) * mm});
            skLineSegment(sketch, "E189.top", {"start": v(82.16, -164.56) * mm, "end": v(102.36, -164.56) * mm});
            skLineSegment(sketch, "E189.left", {"start": v(82.16, -144.36) * mm, "end": v(82.16, -164.56) * mm});
            skLineSegment(sketch, "E189.right", {"start": v(102.36, -144.36) * mm, "end": v(102.36, -164.56) * mm});
            skCircle(sketch, "E190", {"center": v(92.26, -139.46) * mm, "radius": 1.5 * mm, "construction": true});
            skCircle(sketch, "E191", {"center": v(92.26, -169.46) * mm, "radius": 1.5 * mm, "construction": true});
            skPoint(sketch, "E191.centerSnap0", {"position": v(92.26, -164.56) * mm});
            skLineSegment(sketch, "E192.bottom", {"start": v(112.16, -144.36) * mm, "end": v(132.36, -144.36) * mm});
            skLineSegment(sketch, "E192.top", {"start": v(112.16, -164.56) * mm, "end": v(132.36, -164.56) * mm});
            skLineSegment(sketch, "E192.left", {"start": v(112.16, -144.36) * mm, "end": v(112.16, -164.56) * mm});
            skLineSegment(sketch, "E192.right", {"start": v(132.36, -144.36) * mm, "end": v(132.36, -164.56) * mm});
            skCircle(sketch, "E193", {"center": v(122.26, -139.46) * mm, "radius": 1.5 * mm, "construction": true});
            skCircle(sketch, "E194", {"center": v(122.26, -169.46) * mm, "radius": 1.5 * mm, "construction": true});
            skLineSegment(sketch, "E195.bottom", {"start": v(23.26, -145.46) * mm, "end": v(41.26, -145.46) * mm, "construction": true});
            skLineSegment(sketch, "E195.top", {"start": v(23.26, -163.46) * mm, "end": v(41.26, -163.46) * mm, "construction": true});
            skLineSegment(sketch, "E195.left", {"start": v(23.26, -145.46) * mm, "end": v(23.26, -163.46) * mm, "construction": true});
            skLineSegment(sketch, "E195.right", {"start": v(41.26, -145.46) * mm, "end": v(41.26, -163.46) * mm, "construction": true});
            skSolve(sketch);
        }
        {
            var Q0;
            Q0=qSketchRegion(id+"F30",true);
            extrude(context, id + "F31", {"entities" : qUnion([Q0]), "depth" : 11 * mm});
        }
        {
            var Q0;
            Q0=makeQuery(id+"F31.opExtrude","CAP_FACE",FACE,{"disambiguationData":[OSD([sQuery(id+"F30.wireOp",EDGE,"E182.bottom"),sQuery(id+"F30.wireOp",EDGE,"E182.top"),sQuery(id+"F30.wireOp",EDGE,"E182.left"),sQuery(id+"F30.wireOp",EDGE,"E182.right")])],"isStart":true});
            var sketch = newSketch(context, id + "F32", { "sketchPlane" : qUnion([Q0])});
            skLineSegment(sketch, "E196.bottom", {"start": v(16.66, 173.06) * mm, "end": v(136.66, 173.06) * mm});
            skLineSegment(sketch, "E196.top", {"start": v(16.66, 135.86) * mm, "end": v(136.66, 135.86) * mm});
            skLineSegment(sketch, "E196.left", {"start": v(16.66, 173.06) * mm, "end": v(16.66, 135.86) * mm});
            skLineSegment(sketch, "E196.right", {"start": v(136.66, 173.06) * mm, "end": v(136.66, 135.86) * mm});
            skSolve(sketch);
        }
        {
            var Q0;
            Q0=qSketchRegion(id+"F32",true);
            extrude(context, id + "F33", {"entities" : qUnion([Q0]), "operationType" : NewBodyOperationType.REMOVE, "oppositeDirection" : true, "depth" : 8 * mm});
        }
        {
            var Q0;
            Q0=makeQuery(id+"F29.opExtrude","CAP_FACE",FACE,{"disambiguationData":[OSD([sQuery(id+"F28.wireOp",EDGE,"55227c07-3752-4080-a22d-609154aa437d.0"),sQuery(id+"F28.wireOp",EDGE,"55227c07-3752-4080-a22d-609154aa437d.1"),sQuery(id+"F28.wireOp",EDGE,"55227c07-3752-4080-a22d-609154aa437d.2"),sQuery(id+"F28.wireOp",EDGE,"55227c07-3752-4080-a22d-609154aa437d.3"),sQuery(id+"F28.wireOp",EDGE,"E84"),sQuery(id+"F28.wireOp",EDGE,"E86"),sQuery(id+"F28.wireOp",EDGE,"E91.left"),sQuery(id+"F28.wireOp",EDGE,"E91.right"),sQuery(id+"F28.wireOp",EDGE,"E92.left"),sQuery(id+"F28.wireOp",EDGE,"E92.right"),sQuery(id+"F28.wireOp",EDGE,"E93.bottom"),sQuery(id+"F28.wireOp",EDGE,"E93.top"),sQuery(id+"F28.wireOp",EDGE,"E94.trimOffspring"),sQuery(id+"F28.wireOp",EDGE,"E95.trimOffspring"),sQuery(id+"F28.wireOp",EDGE,"E98.trimOffspring"),sQuery(id+"F28.wireOp",EDGE,"E99.trimOffspring"),sQuery(id+"F28.wireOp",EDGE,"E100.trimOffspring"),sQuery(id+"F28.wireOp",EDGE,"E101.trimOffspring"),sQuery(id+"F28.wireOp",EDGE,"E102.trimOffspring"),sQuery(id+"F28.wireOp",EDGE,"E103.trimOffspring"),sQuery(id+"F28.wireOp",EDGE,"E104.bottom"),sQuery(id+"F28.wireOp",EDGE,"E104.left"),sQuery(id+"F28.wireOp",EDGE,"E104.top"),sQuery(id+"F28.wireOp",EDGE,"E104.right"),sQuery(id+"F28.wireOp",EDGE,"E107"),sQuery(id+"F28.wireOp",EDGE,"E109"),sQuery(id+"F28.wireOp",EDGE,"E114.left"),sQuery(id+"F28.wireOp",EDGE,"E114.right"),sQuery(id+"F28.wireOp",EDGE,"E115.left"),sQuery(id+"F28.wireOp",EDGE,"E115.right"),sQuery(id+"F28.wireOp",EDGE,"E116.bottom"),sQuery(id+"F28.wireOp",EDGE,"E116.top"),sQuery(id+"F28.wireOp",EDGE,"E117.trimOffspring"),sQuery(id+"F28.wireOp",EDGE,"E118.trimOffspring"),sQuery(id+"F28.wireOp",EDGE,"E121.trimOffspring"),sQuery(id+"F28.wireOp",EDGE,"E122.trimOffspring"),sQuery(id+"F28.wireOp",EDGE,"E123.trimOffspring"),sQuery(id+"F28.wireOp",EDGE,"E125.trimOffspring"),sQuery(id+"F28.wireOp",EDGE,"E126.trimOffspring"),sQuery(id+"F28.wireOp",EDGE,"E128.trimOffspring"),sQuery(id+"F28.wireOp",EDGE,"E129.bottom"),sQuery(id+"F28.wireOp",EDGE,"E129.left"),sQuery(id+"F28.wireOp",EDGE,"E129.top"),sQuery(id+"F28.wireOp",EDGE,"E129.right"),sQuery(id+"F28.wireOp",EDGE,"E133"),sQuery(id+"F28.wireOp",EDGE,"E135"),sQuery(id+"F28.wireOp",EDGE,"E140.left"),sQuery(id+"F28.wireOp",EDGE,"E140.right"),sQuery(id+"F28.wireOp",EDGE,"E141.left"),sQuery(id+"F28.wireOp",EDGE,"E141.right"),sQuery(id+"F28.wireOp",EDGE,"E142.bottom"),sQuery(id+"F28.wireOp",EDGE,"E142.top"),sQuery(id+"F28.wireOp",EDGE,"E143.trimOffspring"),sQuery(id+"F28.wireOp",EDGE,"E144.trimOffspring"),sQuery(id+"F28.wireOp",EDGE,"E147.trimOffspring"),sQuery(id+"F28.wireOp",EDGE,"E148.trimOffspring"),sQuery(id+"F28.wireOp",EDGE,"E149.trimOffspring"),sQuery(id+"F28.wireOp",EDGE,"E151.trimOffspring"),sQuery(id+"F28.wireOp",EDGE,"E152.trimOffspring"),sQuery(id+"F28.wireOp",EDGE,"E154.trimOffspring"),sQuery(id+"F28.wireOp",EDGE,"E155.bottom"),sQuery(id+"F28.wireOp",EDGE,"E155.left"),sQuery(id+"F28.wireOp",EDGE,"E155.top"),sQuery(id+"F28.wireOp",EDGE,"E155.right"),sQuery(id+"F28.wireOp",EDGE,"E159"),sQuery(id+"F28.wireOp",EDGE,"E161"),sQuery(id+"F28.wireOp",EDGE,"E166.left"),sQuery(id+"F28.wireOp",EDGE,"E166.right"),sQuery(id+"F28.wireOp",EDGE,"E167.left"),sQuery(id+"F28.wireOp",EDGE,"E167.right"),sQuery(id+"F28.wireOp",EDGE,"E168.bottom"),sQuery(id+"F28.wireOp",EDGE,"E168.top"),sQuery(id+"F28.wireOp",EDGE,"E169.trimOffspring"),sQuery(id+"F28.wireOp",EDGE,"E170.trimOffspring"),sQuery(id+"F28.wireOp",EDGE,"E173.trimOffspring"),sQuery(id+"F28.wireOp",EDGE,"E174.trimOffspring"),sQuery(id+"F28.wireOp",EDGE,"E175.trimOffspring"),sQuery(id+"F28.wireOp",EDGE,"E177.trimOffspring"),sQuery(id+"F28.wireOp",EDGE,"E178.trimOffspring"),sQuery(id+"F28.wireOp",EDGE,"E180.trimOffspring"),sQuery(id+"F28.wireOp",EDGE,"E181.bottom"),sQuery(id+"F28.wireOp",EDGE,"E181.top"),sQuery(id+"F28.wireOp",EDGE,"E181.left"),sQuery(id+"F28.wireOp",EDGE,"E181.right")])],"isStart":false});
            var sketch = newSketch(context, id + "F34", { "sketchPlane" : qUnion([Q0])});
            skLineSegment(sketch, "E197.bottom", {"start": v(-94.98, -143.56) * mm, "end": v(-98.98, -143.56) * mm});
            skLineSegment(sketch, "E197.top", {"start": v(-94.98, -161.56) * mm, "end": v(-98.98, -161.56) * mm});
            skLineSegment(sketch, "E197.left", {"start": v(-94.98, -143.56) * mm, "end": v(-94.98, -161.56) * mm});
            skLineSegment(sketch, "E197.right", {"start": v(-98.98, -143.56) * mm, "end": v(-98.98, -161.56) * mm});
            skLineSegment(sketch, "E198.bottom", {"start": v(-76.98, -143.56) * mm, "end": v(-72.98, -143.56) * mm});
            skLineSegment(sketch, "E198.top", {"start": v(-76.98, -161.56) * mm, "end": v(-72.98, -161.56) * mm});
            skLineSegment(sketch, "E198.left", {"start": v(-76.98, -143.56) * mm, "end": v(-76.98, -161.56) * mm});
            skLineSegment(sketch, "E198.right", {"start": v(-72.98, -143.56) * mm, "end": v(-72.98, -161.56) * mm});
            skLineSegment(sketch, "E199.bottom", {"start": v(-64.98, -143.56) * mm, "end": v(-68.98, -143.56) * mm});
            skLineSegment(sketch, "E199.top", {"start": v(-64.98, -161.56) * mm, "end": v(-68.98, -161.56) * mm});
            skLineSegment(sketch, "E199.left", {"start": v(-64.98, -143.56) * mm, "end": v(-64.98, -161.56) * mm});
            skLineSegment(sketch, "E199.right", {"start": v(-68.98, -143.56) * mm, "end": v(-68.98, -161.56) * mm});
            skLineSegment(sketch, "E200.bottom", {"start": v(-46.98, -143.56) * mm, "end": v(-42.98, -143.56) * mm});
            skLineSegment(sketch, "E200.top", {"start": v(-46.98, -161.56) * mm, "end": v(-42.98, -161.56) * mm});
            skLineSegment(sketch, "E200.left", {"start": v(-46.98, -143.56) * mm, "end": v(-46.98, -161.56) * mm});
            skLineSegment(sketch, "E200.right", {"start": v(-42.98, -143.56) * mm, "end": v(-42.98, -161.56) * mm});
            skLineSegment(sketch, "E201.bottom", {"start": v(-34.98, -143.56) * mm, "end": v(-38.98, -143.56) * mm});
            skLineSegment(sketch, "E201.top", {"start": v(-34.98, -161.56) * mm, "end": v(-38.98, -161.56) * mm});
            skLineSegment(sketch, "E201.left", {"start": v(-34.98, -143.56) * mm, "end": v(-34.98, -161.56) * mm});
            skLineSegment(sketch, "E201.right", {"start": v(-38.98, -143.56) * mm, "end": v(-38.98, -161.56) * mm});
            skLineSegment(sketch, "E202.bottom", {"start": v(-16.98, -143.56) * mm, "end": v(-12.98, -143.56) * mm});
            skLineSegment(sketch, "E202.top", {"start": v(-16.98, -161.56) * mm, "end": v(-12.98, -161.56) * mm});
            skLineSegment(sketch, "E202.left", {"start": v(-16.98, -143.56) * mm, "end": v(-16.98, -161.56) * mm});
            skLineSegment(sketch, "E202.right", {"start": v(-12.98, -143.56) * mm, "end": v(-12.98, -161.56) * mm});
            skSolve(sketch);
        }
        {
            var Q0;
            Q0=qSketchRegion(id+"F34",true);
            extrude(context, id + "F35", {"entities" : qUnion([Q0]), "operationType" : NewBodyOperationType.ADD, "depth" : 3 * mm});
        }
        {
            var Q0;
            Q0=makeQuery(id+"F29.opExtrude","CAP_FACE",FACE,{"disambiguationData":[OSD([sQuery(id+"F28.wireOp",EDGE,"55227c07-3752-4080-a22d-609154aa437d.0"),sQuery(id+"F28.wireOp",EDGE,"55227c07-3752-4080-a22d-609154aa437d.1"),sQuery(id+"F28.wireOp",EDGE,"55227c07-3752-4080-a22d-609154aa437d.2"),sQuery(id+"F28.wireOp",EDGE,"55227c07-3752-4080-a22d-609154aa437d.3"),sQuery(id+"F28.wireOp",EDGE,"E84"),sQuery(id+"F28.wireOp",EDGE,"E86"),sQuery(id+"F28.wireOp",EDGE,"E91.left"),sQuery(id+"F28.wireOp",EDGE,"E91.right"),sQuery(id+"F28.wireOp",EDGE,"E92.left"),sQuery(id+"F28.wireOp",EDGE,"E92.right"),sQuery(id+"F28.wireOp",EDGE,"E93.bottom"),sQuery(id+"F28.wireOp",EDGE,"E93.top"),sQuery(id+"F28.wireOp",EDGE,"E94.trimOffspring"),sQuery(id+"F28.wireOp",EDGE,"E95.trimOffspring"),sQuery(id+"F28.wireOp",EDGE,"E98.trimOffspring"),sQuery(id+"F28.wireOp",EDGE,"E99.trimOffspring"),sQuery(id+"F28.wireOp",EDGE,"E100.trimOffspring"),sQuery(id+"F28.wireOp",EDGE,"E101.trimOffspring"),sQuery(id+"F28.wireOp",EDGE,"E102.trimOffspring"),sQuery(id+"F28.wireOp",EDGE,"E103.trimOffspring"),sQuery(id+"F28.wireOp",EDGE,"E104.bottom"),sQuery(id+"F28.wireOp",EDGE,"E104.left"),sQuery(id+"F28.wireOp",EDGE,"E104.top"),sQuery(id+"F28.wireOp",EDGE,"E104.right"),sQuery(id+"F28.wireOp",EDGE,"E107"),sQuery(id+"F28.wireOp",EDGE,"E109"),sQuery(id+"F28.wireOp",EDGE,"E114.left"),sQuery(id+"F28.wireOp",EDGE,"E114.right"),sQuery(id+"F28.wireOp",EDGE,"E115.left"),sQuery(id+"F28.wireOp",EDGE,"E115.right"),sQuery(id+"F28.wireOp",EDGE,"E116.bottom"),sQuery(id+"F28.wireOp",EDGE,"E116.top"),sQuery(id+"F28.wireOp",EDGE,"E117.trimOffspring"),sQuery(id+"F28.wireOp",EDGE,"E118.trimOffspring"),sQuery(id+"F28.wireOp",EDGE,"E121.trimOffspring"),sQuery(id+"F28.wireOp",EDGE,"E122.trimOffspring"),sQuery(id+"F28.wireOp",EDGE,"E123.trimOffspring"),sQuery(id+"F28.wireOp",EDGE,"E125.trimOffspring"),sQuery(id+"F28.wireOp",EDGE,"E126.trimOffspring"),sQuery(id+"F28.wireOp",EDGE,"E128.trimOffspring"),sQuery(id+"F28.wireOp",EDGE,"E129.bottom"),sQuery(id+"F28.wireOp",EDGE,"E129.left"),sQuery(id+"F28.wireOp",EDGE,"E129.top"),sQuery(id+"F28.wireOp",EDGE,"E129.right"),sQuery(id+"F28.wireOp",EDGE,"E133"),sQuery(id+"F28.wireOp",EDGE,"E135"),sQuery(id+"F28.wireOp",EDGE,"E140.left"),sQuery(id+"F28.wireOp",EDGE,"E140.right"),sQuery(id+"F28.wireOp",EDGE,"E141.left"),sQuery(id+"F28.wireOp",EDGE,"E141.right"),sQuery(id+"F28.wireOp",EDGE,"E142.bottom"),sQuery(id+"F28.wireOp",EDGE,"E142.top"),sQuery(id+"F28.wireOp",EDGE,"E143.trimOffspring"),sQuery(id+"F28.wireOp",EDGE,"E144.trimOffspring"),sQuery(id+"F28.wireOp",EDGE,"E147.trimOffspring"),sQuery(id+"F28.wireOp",EDGE,"E148.trimOffspring"),sQuery(id+"F28.wireOp",EDGE,"E149.trimOffspring"),sQuery(id+"F28.wireOp",EDGE,"E151.trimOffspring"),sQuery(id+"F28.wireOp",EDGE,"E152.trimOffspring"),sQuery(id+"F28.wireOp",EDGE,"E154.trimOffspring"),sQuery(id+"F28.wireOp",EDGE,"E155.bottom"),sQuery(id+"F28.wireOp",EDGE,"E155.left"),sQuery(id+"F28.wireOp",EDGE,"E155.top"),sQuery(id+"F28.wireOp",EDGE,"E155.right"),sQuery(id+"F28.wireOp",EDGE,"E159"),sQuery(id+"F28.wireOp",EDGE,"E161"),sQuery(id+"F28.wireOp",EDGE,"E166.left"),sQuery(id+"F28.wireOp",EDGE,"E166.right"),sQuery(id+"F28.wireOp",EDGE,"E167.left"),sQuery(id+"F28.wireOp",EDGE,"E167.right"),sQuery(id+"F28.wireOp",EDGE,"E168.bottom"),sQuery(id+"F28.wireOp",EDGE,"E168.top"),sQuery(id+"F28.wireOp",EDGE,"E169.trimOffspring"),sQuery(id+"F28.wireOp",EDGE,"E170.trimOffspring"),sQuery(id+"F28.wireOp",EDGE,"E173.trimOffspring"),sQuery(id+"F28.wireOp",EDGE,"E174.trimOffspring"),sQuery(id+"F28.wireOp",EDGE,"E175.trimOffspring"),sQuery(id+"F28.wireOp",EDGE,"E177.trimOffspring"),sQuery(id+"F28.wireOp",EDGE,"E178.trimOffspring"),sQuery(id+"F28.wireOp",EDGE,"E180.trimOffspring"),sQuery(id+"F28.wireOp",EDGE,"E181.bottom"),sQuery(id+"F28.wireOp",EDGE,"E181.top"),sQuery(id+"F28.wireOp",EDGE,"E181.left"),sQuery(id+"F28.wireOp",EDGE,"E181.right")])],"isStart":false});
            var sketch = newSketch(context, id + "F36", { "sketchPlane" : qUnion([Q0])});
            skLineSegment(sketch, "E203.bottom", {"start": v(-98.98, -143.56) * mm, "end": v(-72.98, -143.56) * mm});
            skLineSegment(sketch, "E203.top", {"start": v(-98.98, -134.06) * mm, "end": v(-72.98, -134.06) * mm});
            skLineSegment(sketch, "E203.left", {"start": v(-98.98, -143.56) * mm, "end": v(-98.98, -134.06) * mm});
            skLineSegment(sketch, "E203.right", {"start": v(-72.98, -143.56) * mm, "end": v(-72.98, -134.06) * mm});
            skLineSegment(sketch, "E204.bottom", {"start": v(-98.98, -161.56) * mm, "end": v(-72.98, -161.56) * mm});
            skLineSegment(sketch, "E204.top", {"start": v(-98.98, -171.06) * mm, "end": v(-72.98, -171.06) * mm});
            skLineSegment(sketch, "E204.left", {"start": v(-98.98, -161.56) * mm, "end": v(-98.98, -171.06) * mm});
            skLineSegment(sketch, "E204.right", {"start": v(-72.98, -161.56) * mm, "end": v(-72.98, -171.06) * mm});
            skCircle(sketch, "E205", {"center": v(-85.98, -137.56) * mm, "radius": 1.5 * mm});
            skCircle(sketch, "E206", {"center": v(-85.98, -167.56) * mm, "radius": 1.5 * mm});
            skLineSegment(sketch, "E207.bottom", {"start": v(-68.98, -143.56) * mm, "end": v(-42.98, -143.56) * mm});
            skLineSegment(sketch, "E207.top", {"start": v(-68.98, -134.06) * mm, "end": v(-42.98, -134.06) * mm});
            skLineSegment(sketch, "E207.left", {"start": v(-68.98, -143.56) * mm, "end": v(-68.98, -134.06) * mm});
            skLineSegment(sketch, "E207.right", {"start": v(-42.98, -143.56) * mm, "end": v(-42.98, -134.06) * mm});
            skLineSegment(sketch, "E208.bottom", {"start": v(-68.98, -161.56) * mm, "end": v(-42.98, -161.56) * mm});
            skLineSegment(sketch, "E208.top", {"start": v(-68.98, -171.06) * mm, "end": v(-42.98, -171.06) * mm});
            skLineSegment(sketch, "E208.left", {"start": v(-68.98, -161.56) * mm, "end": v(-68.98, -171.06) * mm});
            skLineSegment(sketch, "E208.right", {"start": v(-42.98, -161.56) * mm, "end": v(-42.98, -171.06) * mm});
            skLineSegment(sketch, "E209.bottom", {"start": v(-38.98, -143.56) * mm, "end": v(-12.98, -143.56) * mm});
            skLineSegment(sketch, "E209.top", {"start": v(-38.98, -134.06) * mm, "end": v(-12.98, -134.06) * mm});
            skLineSegment(sketch, "E209.left", {"start": v(-38.98, -143.56) * mm, "end": v(-38.98, -134.06) * mm});
            skLineSegment(sketch, "E209.right", {"start": v(-12.98, -143.56) * mm, "end": v(-12.98, -134.06) * mm});
            skLineSegment(sketch, "E210.bottom", {"start": v(-38.98, -161.56) * mm, "end": v(-12.98, -161.56) * mm});
            skLineSegment(sketch, "E210.top", {"start": v(-38.98, -171.06) * mm, "end": v(-12.98, -171.06) * mm});
            skLineSegment(sketch, "E210.left", {"start": v(-38.98, -161.56) * mm, "end": v(-38.98, -171.06) * mm});
            skLineSegment(sketch, "E210.right", {"start": v(-12.98, -161.56) * mm, "end": v(-12.98, -171.06) * mm});
            skCircle(sketch, "E211", {"center": v(-55.98, -137.56) * mm, "radius": 1.5 * mm});
            skCircle(sketch, "E212", {"center": v(-55.98, -167.56) * mm, "radius": 1.5 * mm});
            skCircle(sketch, "E213", {"center": v(-25.98, -137.56) * mm, "radius": 1.5 * mm});
            skCircle(sketch, "E214", {"center": v(-25.98, -167.56) * mm, "radius": 1.5 * mm});
            skSolve(sketch);
        }
        {
            var Q0;
            Q0=makeQuery(id+"F34.imprint","IMPRINT",FACE,{"disambiguationData":[TD([[makeQuery(id+"F34.imprint","IMPRINT",EDGE,{"derivedFrom":sQuery(id+"F34.wireOp",EDGE,"E197.bottom")}),-1.0]])]});
            var sketch = newSketch(context, id + "F37", { "sketchPlane" : qUnion([Q0])});
            skLineSegment(sketch, "E215.bottom", {"start": v(-124.73, -151.56) * mm, "end": v(-121.73, -151.56) * mm});
            skLineSegment(sketch, "E215.top", {"start": v(-124.73, -153.56) * mm, "end": v(-121.73, -153.56) * mm});
            skLineSegment(sketch, "E215.left", {"start": v(-124.73, -151.56) * mm, "end": v(-124.73, -153.56) * mm});
            skLineSegment(sketch, "E215.right", {"start": v(-121.73, -151.56) * mm, "end": v(-121.73, -153.56) * mm});
            skLineSegment(sketch, "E216.bottom", {"start": v(-110.23, -151.56) * mm, "end": v(-107.23, -151.56) * mm});
            skLineSegment(sketch, "E216.top", {"start": v(-110.23, -153.56) * mm, "end": v(-107.23, -153.56) * mm});
            skLineSegment(sketch, "E216.left", {"start": v(-110.23, -151.56) * mm, "end": v(-110.23, -153.56) * mm});
            skLineSegment(sketch, "E216.right", {"start": v(-107.23, -151.56) * mm, "end": v(-107.23, -153.56) * mm});
            skSolve(sketch);
        }
        {
            var Q0;
            Q0=qSketchRegion(id+"F37",true);
            extrude(context, id + "F38", {"entities" : qUnion([Q0]), "operationType" : NewBodyOperationType.ADD, "depth" : 9 * mm});
        }
        {
            var Q0;
            Q0=makeQuery(id+"F34.imprint","IMPRINT",FACE,{"disambiguationData":[TD([[makeQuery(id+"F34.imprint","IMPRINT",EDGE,{"derivedFrom":sQuery(id+"F34.wireOp",EDGE,"E197.bottom")}),-1.0]])]});
            var sketch = newSketch(context, id + "F39", { "sketchPlane" : qUnion([Q0])});
            skLineSegment(sketch, "E217.bottom", {"start": v(-118.48, -151.56) * mm, "end": v(-113.48, -151.56) * mm});
            skLineSegment(sketch, "E217.top", {"start": v(-118.48, -153.56) * mm, "end": v(-113.48, -153.56) * mm});
            skLineSegment(sketch, "E217.left", {"start": v(-118.48, -151.56) * mm, "end": v(-118.48, -153.56) * mm});
            skLineSegment(sketch, "E217.right", {"start": v(-113.48, -151.56) * mm, "end": v(-113.48, -153.56) * mm});
            skSolve(sketch);
        }
        {
            var Q0;
            Q0=qSketchRegion(id+"F39",true);
            extrude(context, id + "F40", {"entities" : qUnion([Q0]), "operationType" : NewBodyOperationType.ADD, "depth" : 3 * mm});
        }
        {
            var Q0;
            Q0=makeQuery(id+"F31.opExtrude","SWEPT_EDGE",EDGE,{"disambiguationData":[OSD([sQuery(id+"F30.wireOp",EDGE,"E182.bottom"),sQuery(id+"F30.wireOp",EDGE,"E182.left")])]});
            var Q1;
            Q1=makeQuery(id+"F31.opExtrude","SWEPT_EDGE",EDGE,{"disambiguationData":[OSD([sQuery(id+"F30.wireOp",EDGE,"E182.top"),sQuery(id+"F30.wireOp",EDGE,"E182.left")])]});
            var Q2;
            Q2=makeQuery(id+"F31.opExtrude","SWEPT_EDGE",EDGE,{"disambiguationData":[OSD([sQuery(id+"F30.wireOp",EDGE,"E182.top"),sQuery(id+"F30.wireOp",EDGE,"E182.right")])]});
            var Q3;
            Q3=makeQuery(id+"F31.opExtrude","SWEPT_EDGE",EDGE,{"disambiguationData":[OSD([sQuery(id+"F30.wireOp",EDGE,"E182.bottom"),sQuery(id+"F30.wireOp",EDGE,"E182.right")])]});
            var Q4;
            Q4=makeQuery(id+"F31.opExtrude","CAP_EDGE",EDGE,{"disambiguationData":[OSD([sQuery(id+"F30.wireOp",EDGE,"E182.top")])],"isStart":false});
            var Q5;
            Q5=makeQuery(id+"F31.opExtrude","CAP_EDGE",EDGE,{"disambiguationData":[OSD([sQuery(id+"F30.wireOp",EDGE,"E182.left")])],"isStart":false});
            var Q6;
            Q6=makeQuery(id+"F31.opExtrude","CAP_EDGE",EDGE,{"disambiguationData":[OSD([sQuery(id+"F30.wireOp",EDGE,"E182.bottom")])],"isStart":false});
            var Q7;
            Q7=makeQuery(id+"F31.opExtrude","CAP_EDGE",EDGE,{"disambiguationData":[OSD([sQuery(id+"F30.wireOp",EDGE,"E182.right")])],"isStart":false});
            fillet(context, id + "F41", {"entities" : qUnion([Q0, Q1, Q2, Q3, Q4, Q5, Q6, Q7]), "radius" : 1 * mm, "tangentPropagation" : true, "allowEdgeOverflow" : false});
        }
        {
            var Q0;
            Q0=makeQuery(id+"F8.opExtrude","SWEPT_EDGE",EDGE,{"disambiguationData":[OSD([sQuery(id+"F7.wireOp",EDGE,"E14.top"),sQuery(id+"F7.wireOp",EDGE,"E14.right")])]});
            var Q1;
            Q1=makeQuery(id+"F8.opExtrude","CAP_EDGE",EDGE,{"disambiguationData":[OSD([sQuery(id+"F7.wireOp",EDGE,"E14.top")])],"isStart":false});
            var Q2;
            Q2=makeQuery(id+"F8.opExtrude","CAP_EDGE",EDGE,{"disambiguationData":[OSD([sQuery(id+"F7.wireOp",EDGE,"E14.right")])],"isStart":false});
            var Q3;
            Q3=makeQuery(id+"F8.opExtrude","SWEPT_EDGE",EDGE,{"disambiguationData":[OSD([sQuery(id+"F7.wireOp",EDGE,"E14.bottom"),sQuery(id+"F7.wireOp",EDGE,"E14.right")])]});
            var Q4;
            Q4=makeQuery(id+"F8.opExtrude","CAP_EDGE",EDGE,{"disambiguationData":[OSD([sQuery(id+"F7.wireOp",EDGE,"E14.bottom")])],"isStart":false});
            var Q5;
            Q5=makeQuery(id+"F8.opExtrude","SWEPT_EDGE",EDGE,{"disambiguationData":[OSD([sQuery(id+"F7.wireOp",EDGE,"E14.bottom"),sQuery(id+"F7.wireOp",EDGE,"E14.left")])]});
            var Q6;
            Q6=makeQuery(id+"F8.opExtrude","CAP_EDGE",EDGE,{"disambiguationData":[OSD([sQuery(id+"F7.wireOp",EDGE,"E14.left")])],"isStart":false});
            var Q7;
            Q7=makeQuery(id+"F8.opExtrude","SWEPT_EDGE",EDGE,{"disambiguationData":[OSD([sQuery(id+"F7.wireOp",EDGE,"E14.top"),sQuery(id+"F7.wireOp",EDGE,"E14.left")])]});
            var Q8;
            Q8=makeQuery(id+"F1.opExtrude","SWEPT_EDGE",EDGE,{"disambiguationData":[OSD([sQuery(id+"F0.wireOp",EDGE,"E1.bottom"),sQuery(id+"F0.wireOp",EDGE,"E1.right")])]});
            var Q9;
            Q9=makeQuery(id+"F1.opExtrude","CAP_EDGE",EDGE,{"disambiguationData":[OSD([sQuery(id+"F0.wireOp",EDGE,"E1.bottom")])],"isStart":false});
            var Q10;
            Q10=makeQuery(id+"F1.opExtrude","SWEPT_EDGE",EDGE,{"disambiguationData":[OSD([sQuery(id+"F0.wireOp",EDGE,"E1.bottom"),sQuery(id+"F0.wireOp",EDGE,"E1.left")])]});
            var Q11;
            Q11=makeQuery(id+"F1.opExtrude","CAP_EDGE",EDGE,{"disambiguationData":[OSD([sQuery(id+"F0.wireOp",EDGE,"E1.right")])],"isStart":false});
            var Q12;
            Q12=makeQuery(id+"F1.opExtrude","SWEPT_EDGE",EDGE,{"disambiguationData":[OSD([sQuery(id+"F0.wireOp",EDGE,"E1.top"),sQuery(id+"F0.wireOp",EDGE,"E1.right")])]});
            var Q13;
            Q13=makeQuery(id+"F1.opExtrude","CAP_EDGE",EDGE,{"disambiguationData":[OSD([sQuery(id+"F0.wireOp",EDGE,"E1.top")])],"isStart":false});
            var Q14;
            Q14=makeQuery(id+"F1.opExtrude","SWEPT_EDGE",EDGE,{"disambiguationData":[OSD([sQuery(id+"F0.wireOp",EDGE,"E1.top"),sQuery(id+"F0.wireOp",EDGE,"E1.left")])]});
            var Q15;
            Q15=makeQuery(id+"F1.opExtrude","CAP_EDGE",EDGE,{"disambiguationData":[OSD([sQuery(id+"F0.wireOp",EDGE,"E1.left")])],"isStart":false});
            fillet(context, id + "F42", {"entities" : qUnion([Q0, Q1, Q2, Q3, Q4, Q5, Q6, Q7, Q8, Q9, Q10, Q11, Q12, Q13, Q14, Q15]), "radius" : 0.5 * mm, "tangentPropagation" : true, "allowEdgeOverflow" : false});
        }
        {
            var Q0;
            Q0=makeQuery(id+"F36.imprint","IMPRINT",FACE,{"disambiguationData":[TD([[makeQuery(id+"F36.imprint","IMPRINT",EDGE,{"derivedFrom":sQuery(id+"F36.wireOp",EDGE,"E203.top")}),-1.0]])]});
            var Q1;
            Q1=makeQuery(id+"F36.imprint","IMPRINT",FACE,{"disambiguationData":[TD([[makeQuery(id+"F36.imprint","IMPRINT",EDGE,{"derivedFrom":sQuery(id+"F36.wireOp",EDGE,"E204.top")}),1.0]])]});
            var Q2;
            Q2=makeQuery(id+"F36.imprint","IMPRINT",FACE,{"disambiguationData":[TD([[makeQuery(id+"F36.imprint","IMPRINT",EDGE,{"derivedFrom":sQuery(id+"F36.wireOp",EDGE,"E208.top")}),1.0]])]});
            var Q3;
            Q3=makeQuery(id+"F36.imprint","IMPRINT",FACE,{"disambiguationData":[TD([[makeQuery(id+"F36.imprint","IMPRINT",EDGE,{"derivedFrom":sQuery(id+"F36.wireOp",EDGE,"E207.top")}),-1.0]])]});
            var Q4;
            Q4=makeQuery(id+"F36.imprint","IMPRINT",FACE,{"disambiguationData":[TD([[makeQuery(id+"F36.imprint","IMPRINT",EDGE,{"derivedFrom":sQuery(id+"F36.wireOp",EDGE,"E209.top")}),-1.0]])]});
            var Q5;
            Q5=makeQuery(id+"F36.imprint","IMPRINT",FACE,{"disambiguationData":[TD([[makeQuery(id+"F36.imprint","IMPRINT",EDGE,{"derivedFrom":sQuery(id+"F36.wireOp",EDGE,"E210.top")}),1.0]])]});
            extrude(context, id + "F43", {"entities" : qUnion([Q0, Q1, Q2, Q3, Q4, Q5]), "operationType" : NewBodyOperationType.ADD, "depth" : 3 * mm});
        }
        {
            var Q0;
            Q0=makeQuery(id+"F29.opExtrude","SWEPT_FACE",FACE,{"disambiguationData":[OSD([sQuery(id+"F28.wireOp",EDGE,"E181.left")])]});
            extrude(context, id + "F44", {"entities" : qUnion([Q0]), "operationType" : NewBodyOperationType.ADD, "depth" : 2 * mm});
        }
        {
            var Q0;
            {var subQ0=sQuery(id+"F28.wireOp",EDGE,"E181.left");var subQ1=sQuery(id+"F28.wireOp",EDGE,"55227c07-3752-4080-a22d-609154aa437d.3");var subQ2=sQuery(id+"F28.wireOp",EDGE,"55227c07-3752-4080-a22d-609154aa437d.0");var subQ4=sQuery(id+"F28.wireOp",EDGE,"E102.trimOffspring");var subQ6=sQuery(id+"F28.wireOp",EDGE,"E181.top");var subQ7=sQuery(id+"F28.wireOp",EDGE,"E103.trimOffspring");var subQ8=sQuery(id+"F28.wireOp",EDGE,"55227c07-3752-4080-a22d-609154aa437d.2");var subQ11=sQuery(id+"F28.wireOp",EDGE,"E101.trimOffspring");var subQ13=sQuery(id+"F28.wireOp",EDGE,"E181.bottom");var subQ14=sQuery(id+"F28.wireOp",EDGE,"E95.trimOffspring");var subQ16=sQuery(id+"F28.wireOp",EDGE,"E100.trimOffspring");var subQ17=sQuery(id+"F28.wireOp",EDGE,"E99.trimOffspring");var subQ18=sQuery(id+"F28.wireOp",EDGE,"55227c07-3752-4080-a22d-609154aa437d.1");var subQ21=sQuery(id+"F28.wireOp",EDGE,"E93.bottom");var subQ22=sQuery(id+"F28.wireOp",EDGE,"E92.right");var subQ24=sQuery(id+"F28.wireOp",EDGE,"E91.right");var subQ26=sQuery(id+"F28.wireOp",EDGE,"E92.left");var subQ28=sQuery(id+"F28.wireOp",EDGE,"E94.trimOffspring");var subQ29=sQuery(id+"F28.wireOp",EDGE,"E93.top");var subQ30=sQuery(id+"F28.wireOp",EDGE,"E91.left");var subQ31=sQuery(id+"F28.wireOp",EDGE,"E84");var subQ32=sQuery(id+"F28.wireOp",EDGE,"E86");var subQ33=sQuery(id+"F28.wireOp",EDGE,"E98.trimOffspring");Q0=makeQuery(id+"F44.boolean.opBoolean","MERGE",FACE,{"derivedFrom":[makeQuery(id+"F43.boolean.opBoolean","SPLIT",FACE,{"disambiguationData":[TD([makeQuery(id+"F29.opExtrude","SWEPT_FACE",FACE,{"disambiguationData":[OSD([subQ31])]})])],"derivedFrom":makeQuery(id+"F29.opExtrude","CAP_FACE",FACE,{"disambiguationData":[OSD([subQ2,subQ18,subQ8,subQ1,subQ31,subQ32,subQ30,subQ24,subQ26,subQ22,subQ21,subQ29,subQ28,subQ14,subQ33,subQ17,subQ16,subQ11,subQ4,subQ7,sQuery(id+"F28.wireOp",EDGE,"E104.bottom"),sQuery(id+"F28.wireOp",EDGE,"E104.left"),sQuery(id+"F28.wireOp",EDGE,"E104.top"),sQuery(id+"F28.wireOp",EDGE,"E104.right"),sQuery(id+"F28.wireOp",EDGE,"E107"),sQuery(id+"F28.wireOp",EDGE,"E109"),sQuery(id+"F28.wireOp",EDGE,"E114.left"),sQuery(id+"F28.wireOp",EDGE,"E114.right"),sQuery(id+"F28.wireOp",EDGE,"E115.left"),sQuery(id+"F28.wireOp",EDGE,"E115.right"),sQuery(id+"F28.wireOp",EDGE,"E116.bottom"),sQuery(id+"F28.wireOp",EDGE,"E116.top"),sQuery(id+"F28.wireOp",EDGE,"E117.trimOffspring"),sQuery(id+"F28.wireOp",EDGE,"E118.trimOffspring"),sQuery(id+"F28.wireOp",EDGE,"E121.trimOffspring"),sQuery(id+"F28.wireOp",EDGE,"E122.trimOffspring"),sQuery(id+"F28.wireOp",EDGE,"E123.trimOffspring"),sQuery(id+"F28.wireOp",EDGE,"E125.trimOffspring"),sQuery(id+"F28.wireOp",EDGE,"E126.trimOffspring"),sQuery(id+"F28.wireOp",EDGE,"E128.trimOffspring"),sQuery(id+"F28.wireOp",EDGE,"E129.bottom"),sQuery(id+"F28.wireOp",EDGE,"E129.left"),sQuery(id+"F28.wireOp",EDGE,"E129.top"),sQuery(id+"F28.wireOp",EDGE,"E129.right"),sQuery(id+"F28.wireOp",EDGE,"E133"),sQuery(id+"F28.wireOp",EDGE,"E135"),sQuery(id+"F28.wireOp",EDGE,"E140.left"),sQuery(id+"F28.wireOp",EDGE,"E140.right"),sQuery(id+"F28.wireOp",EDGE,"E141.left"),sQuery(id+"F28.wireOp",EDGE,"E141.right"),sQuery(id+"F28.wireOp",EDGE,"E142.bottom"),sQuery(id+"F28.wireOp",EDGE,"E142.top"),sQuery(id+"F28.wireOp",EDGE,"E143.trimOffspring"),sQuery(id+"F28.wireOp",EDGE,"E144.trimOffspring"),sQuery(id+"F28.wireOp",EDGE,"E147.trimOffspring"),sQuery(id+"F28.wireOp",EDGE,"E148.trimOffspring"),sQuery(id+"F28.wireOp",EDGE,"E149.trimOffspring"),sQuery(id+"F28.wireOp",EDGE,"E151.trimOffspring"),sQuery(id+"F28.wireOp",EDGE,"E152.trimOffspring"),sQuery(id+"F28.wireOp",EDGE,"E154.trimOffspring"),sQuery(id+"F28.wireOp",EDGE,"E155.bottom"),sQuery(id+"F28.wireOp",EDGE,"E155.left"),sQuery(id+"F28.wireOp",EDGE,"E155.top"),sQuery(id+"F28.wireOp",EDGE,"E155.right"),sQuery(id+"F28.wireOp",EDGE,"E159"),sQuery(id+"F28.wireOp",EDGE,"E161"),sQuery(id+"F28.wireOp",EDGE,"E166.left"),sQuery(id+"F28.wireOp",EDGE,"E166.right"),sQuery(id+"F28.wireOp",EDGE,"E167.left"),sQuery(id+"F28.wireOp",EDGE,"E167.right"),sQuery(id+"F28.wireOp",EDGE,"E168.bottom"),sQuery(id+"F28.wireOp",EDGE,"E168.top"),sQuery(id+"F28.wireOp",EDGE,"E169.trimOffspring"),sQuery(id+"F28.wireOp",EDGE,"E170.trimOffspring"),sQuery(id+"F28.wireOp",EDGE,"E173.trimOffspring"),sQuery(id+"F28.wireOp",EDGE,"E174.trimOffspring"),sQuery(id+"F28.wireOp",EDGE,"E175.trimOffspring"),sQuery(id+"F28.wireOp",EDGE,"E177.trimOffspring"),sQuery(id+"F28.wireOp",EDGE,"E178.trimOffspring"),sQuery(id+"F28.wireOp",EDGE,"E180.trimOffspring"),subQ13,subQ6,subQ0,sQuery(id+"F28.wireOp",EDGE,"E181.right")])],"isStart":false})}),makeQuery(id+"F44.opExtrude","SWEPT_FACE",FACE,{"disambiguationData":[OSD([subQ0]),TDD([makeQuery(id+"F29.opExtrude","CAP_EDGE",EDGE,{"disambiguationData":[OSD([subQ0])],"isStart":false})])]})]});}
            var sketch = newSketch(context, id + "F45", { "sketchPlane" : qUnion([Q0])});
            skLineSegment(sketch, "E218.bottom", {"start": v(-131.58, -134.06) * mm, "end": v(-129.58, -134.06) * mm});
            skLineSegment(sketch, "E218.top", {"start": v(-131.58, -171.06) * mm, "end": v(-129.58, -171.06) * mm});
            skLineSegment(sketch, "E218.left", {"start": v(-131.58, -134.06) * mm, "end": v(-131.58, -171.06) * mm});
            skLineSegment(sketch, "E218.right", {"start": v(-129.58, -134.06) * mm, "end": v(-129.58, -171.06) * mm});
            skSolve(sketch);
        }
        {
            var Q0;
            Q0=qSketchRegion(id+"F45",true);
            extrude(context, id + "F46", {"entities" : qUnion([Q0]), "operationType" : NewBodyOperationType.ADD, "depth" : 7 * mm});
        }
        {
            var Q0;
            Q0=makeQuery(id+"F33.boolean.opBoolean","COPY",FACE,{"derivedFrom":makeQuery(id+"F33.opExtrude","CAP_FACE",FACE,{"disambiguationData":[OSD([sQuery(id+"F32.wireOp",EDGE,"E196.bottom"),sQuery(id+"F32.wireOp",EDGE,"E196.top"),sQuery(id+"F32.wireOp",EDGE,"E196.left"),sQuery(id+"F32.wireOp",EDGE,"E196.right")])],"isStart":false})});
            var sketch = newSketch(context, id + "F47", { "sketchPlane" : qUnion([Q0])});
            skLineSegment(sketch, "E219.bottom", {"start": v(22.06, 164.66) * mm, "end": v(42.46, 164.66) * mm});
            skLineSegment(sketch, "E219.top", {"start": v(22.06, 173.06) * mm, "end": v(42.46, 173.06) * mm});
            skLineSegment(sketch, "E219.left", {"start": v(22.06, 164.66) * mm, "end": v(22.06, 173.06) * mm});
            skLineSegment(sketch, "E219.right", {"start": v(42.46, 164.66) * mm, "end": v(42.46, 173.06) * mm});
            skLineSegment(sketch, "E220.bottom", {"start": v(22.06, 144.26) * mm, "end": v(42.46, 144.26) * mm});
            skLineSegment(sketch, "E220.top", {"start": v(22.06, 135.86) * mm, "end": v(42.46, 135.86) * mm});
            skLineSegment(sketch, "E220.left", {"start": v(22.06, 144.26) * mm, "end": v(22.06, 135.86) * mm});
            skLineSegment(sketch, "E220.right", {"start": v(42.46, 144.26) * mm, "end": v(42.46, 135.86) * mm});
            skSolve(sketch);
        }
        {
            var Q0;
            Q0=qSketchRegion(id+"F47",true);
            extrude(context, id + "F48", {"entities" : qUnion([Q0]), "operationType" : NewBodyOperationType.ADD, "depth" : 3 * mm});
        }
        {
            var Q0;
            Q0=makeQuery(id+"F31.opExtrude","SWEPT_FACE",FACE,{"disambiguationData":[OSD([sQuery(id+"F30.wireOp",EDGE,"E182.left")])]});
            var sketch = newSketch(context, id + "F49", { "sketchPlane" : qUnion([Q0])});
            skCircle(sketch, "E221", {"center": v(139.86, 5.5) * mm, "radius": 1.5 * mm});
            skCircle(sketch, "E222", {"center": v(169.06, 5.5) * mm, "radius": 1.5 * mm});
            skSolve(sketch);
        }
        {
            var Q0;
            Q0=qSketchRegion(id+"F49",true);
            extrude(context, id + "F50", {"entities" : qUnion([Q0]), "operationType" : NewBodyOperationType.REMOVE, "oppositeDirection" : true, "depth" : 3 * mm});
        }
        {
            var Q0;
            Q0=makeQuery(id+"F46.boolean.opBoolean","MERGE",FACE,{"derivedFrom":[makeQuery(id+"F44.opExtrude","CAP_FACE",FACE,{"disambiguationData":[OSD([sQuery(id+"F28.wireOp",EDGE,"E181.left")])],"isStart":false}),makeQuery(id+"F46.opExtrude","SWEPT_FACE",FACE,{"disambiguationData":[OSD([sQuery(id+"F45.wireOp",EDGE,"E218.left")])]})]});
            var sketch = newSketch(context, id + "F51", { "sketchPlane" : qUnion([Q0])});
            skCircle(sketch, "E223", {"center": v(137.96, 5.5) * mm, "radius": 1.2 * mm});
            skCircle(sketch, "E224", {"center": v(167.16, 5.5) * mm, "radius": 1.2 * mm});
            skSolve(sketch);
        }
        {
            var Q0;
            Q0=makeQuery(id+"F31.opExtrude","SWEPT_FACE",FACE,{"disambiguationData":[OSD([sQuery(id+"F30.wireOp",EDGE,"E182.right")])]});
            var sketch = newSketch(context, id + "F52", { "sketchPlane" : qUnion([Q0])});
            skCircle(sketch, "E225", {"center": v(-169.06, 5.5) * mm, "radius": 1.5 * mm});
            skCircle(sketch, "E226", {"center": v(-139.86, 5.5) * mm, "radius": 1.5 * mm});
            skSolve(sketch);
        }
        {
            var Q0;
            Q0=makeQuery(id+"F52.imprint","IMPRINT",FACE,{"disambiguationData":[TD([[makeQuery(id+"F52.imprint","IMPRINT",EDGE,{"derivedFrom":sQuery(id+"F52.wireOp",EDGE,"E225")}),1.0]])]});
            var Q1;
            Q1=makeQuery(id+"F52.imprint","IMPRINT",FACE,{"disambiguationData":[TD([[makeQuery(id+"F52.imprint","IMPRINT",EDGE,{"derivedFrom":sQuery(id+"F52.wireOp",EDGE,"E226")}),1.0]])]});
            extrude(context, id + "F53", {"entities" : qUnion([Q0, Q1]), "operationType" : NewBodyOperationType.REMOVE, "oppositeDirection" : true, "depth" : 2 * mm});
        }
        {
            var Q0;
            {var subQ0=sQuery(id+"F32.wireOp",EDGE,"E196.top");var subQ1=sQuery(id+"F32.wireOp",EDGE,"E196.bottom");var subQ2=sQuery(id+"F32.wireOp",EDGE,"E196.right");Q0=makeQuery(id+"F48.boolean.opBoolean","SPLIT",FACE,{"disambiguationData":[TD([makeQuery(id+"F31.opExtrude","SWEPT_FACE",FACE,{"disambiguationData":[OSD([sQuery(id+"F30.wireOp",EDGE,"E183.right")])]})])],"derivedFrom":makeQuery(id+"F33.boolean.opBoolean","COPY",FACE,{"derivedFrom":makeQuery(id+"F33.opExtrude","CAP_FACE",FACE,{"disambiguationData":[OSD([subQ1,subQ0,sQuery(id+"F32.wireOp",EDGE,"E196.left"),subQ2])],"isStart":false})})});}
            var sketch = newSketch(context, id + "F54", { "sketchPlane" : qUnion([Q0])});
            skLineSegment(sketch, "E227.bottom", {"start": v(45.96, 173.06) * mm, "end": v(48.96, 173.06) * mm});
            skLineSegment(sketch, "E227.top", {"start": v(45.96, 135.86) * mm, "end": v(48.96, 135.86) * mm});
            skLineSegment(sketch, "E227.left", {"start": v(45.96, 173.06) * mm, "end": v(45.96, 135.86) * mm});
            skLineSegment(sketch, "E227.right", {"start": v(48.96, 173.06) * mm, "end": v(48.96, 135.86) * mm});
            skLineSegment(sketch, "E228.bottom", {"start": v(75.86, 173.06) * mm, "end": v(78.86, 173.06) * mm});
            skLineSegment(sketch, "E228.top", {"start": v(75.86, 135.86) * mm, "end": v(78.86, 135.86) * mm});
            skLineSegment(sketch, "E228.left", {"start": v(75.86, 173.06) * mm, "end": v(75.86, 135.86) * mm});
            skLineSegment(sketch, "E228.right", {"start": v(78.86, 173.06) * mm, "end": v(78.86, 135.86) * mm});
            skLineSegment(sketch, "E229.bottom", {"start": v(105.86, 173.06) * mm, "end": v(108.86, 173.06) * mm});
            skLineSegment(sketch, "E229.top", {"start": v(105.86, 135.86) * mm, "end": v(108.86, 135.86) * mm});
            skLineSegment(sketch, "E229.left", {"start": v(105.86, 173.06) * mm, "end": v(105.86, 135.86) * mm});
            skLineSegment(sketch, "E229.right", {"start": v(108.86, 173.06) * mm, "end": v(108.86, 135.86) * mm});
            skSolve(sketch);
        }
        {
            var Q0;
            Q0=qSketchRegion(id+"F54",true);
            extrude(context, id + "F55", {"entities" : qUnion([Q0]), "operationType" : NewBodyOperationType.ADD, "depth" : 1 * mm});
        }
        {
            var Q0;
            Q0=makeQuery(id+"F43.boolean.opBoolean","MERGE",FACE,{"derivedFrom":[makeQuery(id+"F35.opExtrude","SWEPT_FACE",FACE,{"disambiguationData":[OSD([sQuery(id+"F34.wireOp",EDGE,"E202.right")])]}),makeQuery(id+"F43.opExtrude","SWEPT_FACE",FACE,{"disambiguationData":[OSD([sQuery(id+"F36.wireOp",EDGE,"E209.right")])]}),makeQuery(id+"F43.opExtrude","SWEPT_FACE",FACE,{"disambiguationData":[OSD([sQuery(id+"F36.wireOp",EDGE,"E210.right")])]})]});
            extrude(context, id + "F56", {"entities" : qUnion([Q0]), "operationType" : NewBodyOperationType.ADD, "depth" : 1 * mm});
        }
        {
            var Q0;
            {var subQ0=sQuery(id+"F36.wireOp",EDGE,"E210.right");var subQ1=sQuery(id+"F36.wireOp",EDGE,"E209.right");var subQ2=sQuery(id+"F34.wireOp",EDGE,"E202.right");Q0=makeQuery(id+"F56.boolean.opBoolean","MERGE",FACE,{"derivedFrom":[makeQuery(id+"F43.boolean.opBoolean","MERGE",FACE,{"derivedFrom":[makeQuery(id+"F35.opExtrude","CAP_FACE",FACE,{"disambiguationData":[OSD([sQuery(id+"F34.wireOp",EDGE,"E201.bottom"),sQuery(id+"F34.wireOp",EDGE,"E201.top"),sQuery(id+"F34.wireOp",EDGE,"E201.left"),sQuery(id+"F34.wireOp",EDGE,"E201.right")])],"isStart":false}),makeQuery(id+"F35.opExtrude","CAP_FACE",FACE,{"disambiguationData":[OSD([sQuery(id+"F34.wireOp",EDGE,"E202.bottom"),sQuery(id+"F34.wireOp",EDGE,"E202.top"),sQuery(id+"F34.wireOp",EDGE,"E202.left"),subQ2])],"isStart":false}),makeQuery(id+"F43.opExtrude","CAP_FACE",FACE,{"disambiguationData":[OSD([sQuery(id+"F36.wireOp",EDGE,"E209.bottom"),sQuery(id+"F36.wireOp",EDGE,"E209.top"),sQuery(id+"F36.wireOp",EDGE,"E209.left"),subQ1,sQuery(id+"F36.wireOp",EDGE,"E213")])],"isStart":false}),makeQuery(id+"F43.opExtrude","CAP_FACE",FACE,{"disambiguationData":[OSD([sQuery(id+"F36.wireOp",EDGE,"E210.bottom"),sQuery(id+"F36.wireOp",EDGE,"E210.top"),sQuery(id+"F36.wireOp",EDGE,"E210.left"),subQ0,sQuery(id+"F36.wireOp",EDGE,"E214")])],"isStart":false})]}),makeQuery(id+"F56.opExtrude","SWEPT_FACE",FACE,{"disambiguationData":[OSD([subQ2,subQ1,subQ0]),TDD([makeQuery(id+"F43.boolean.opBoolean","MERGE",EDGE,{"derivedFrom":[makeQuery(id+"F35.opExtrude","CAP_EDGE",EDGE,{"disambiguationData":[OSD([subQ2])],"isStart":false}),makeQuery(id+"F43.opExtrude","CAP_EDGE",EDGE,{"disambiguationData":[OSD([subQ1])],"isStart":false}),makeQuery(id+"F43.opExtrude","CAP_EDGE",EDGE,{"disambiguationData":[OSD([subQ0])],"isStart":false})]})])]})]});}
            var sketch = newSketch(context, id + "F57", { "sketchPlane" : qUnion([Q0])});
            skLineSegment(sketch, "E230.bottom", {"start": v(-11.98, -171.06) * mm, "end": v(-13.98, -171.06) * mm});
            skLineSegment(sketch, "E230.top", {"start": v(-11.98, -134.06) * mm, "end": v(-13.98, -134.06) * mm});
            skLineSegment(sketch, "E230.left", {"start": v(-11.98, -171.06) * mm, "end": v(-11.98, -134.06) * mm});
            skLineSegment(sketch, "E230.right", {"start": v(-13.98, -171.06) * mm, "end": v(-13.98, -134.06) * mm});
            skSolve(sketch);
        }
        {
            var Q0;
            Q0=qSketchRegion(id+"F57",true);
            extrude(context, id + "F58", {"entities" : qUnion([Q0]), "operationType" : NewBodyOperationType.ADD, "depth" : 4 * mm});
        }
        {
            var Q0;
            Q0=qSketchRegion(id+"F51",true);
            extrude(context, id + "F59", {"entities" : qUnion([Q0]), "operationType" : NewBodyOperationType.REMOVE, "endBound" : BoundingType.THROUGH_ALL, "oppositeDirection" : true, "depth" : 3 * mm});
        }
        {
            var Q0;
            Q0=qSketchRegion(id+"F54",true);
            extrude(context, id + "F60", {"entities" : qUnion([Q0]), "operationType" : NewBodyOperationType.ADD, "depth" : 3 * mm});
        }
        {
            var Q0;
            Q0=makeQuery(id+"F43.boolean.opBoolean","MERGE",FACE,{"derivedFrom":[makeQuery(id+"F35.opExtrude","SWEPT_FACE",FACE,{"disambiguationData":[OSD([sQuery(id+"F34.wireOp",EDGE,"E198.right")])]}),makeQuery(id+"F43.opExtrude","SWEPT_FACE",FACE,{"disambiguationData":[OSD([sQuery(id+"F36.wireOp",EDGE,"E203.right")])]}),makeQuery(id+"F43.opExtrude","SWEPT_FACE",FACE,{"disambiguationData":[OSD([sQuery(id+"F36.wireOp",EDGE,"E204.right")])]})]});
            var Q1;
            Q1=makeQuery(id+"F43.boolean.opBoolean","MERGE",FACE,{"derivedFrom":[makeQuery(id+"F35.opExtrude","SWEPT_FACE",FACE,{"disambiguationData":[OSD([sQuery(id+"F34.wireOp",EDGE,"E200.right")])]}),makeQuery(id+"F43.opExtrude","SWEPT_FACE",FACE,{"disambiguationData":[OSD([sQuery(id+"F36.wireOp",EDGE,"E207.right")])]}),makeQuery(id+"F43.opExtrude","SWEPT_FACE",FACE,{"disambiguationData":[OSD([sQuery(id+"F36.wireOp",EDGE,"E208.right")])]})]});
            extrude(context, id + "F61", {"entities" : qUnion([Q0, Q1]), "operationType" : NewBodyOperationType.ADD, "depth" : 5 * mm});
        }
        {
            var Q0;
            Q0=makeQuery(id+"F28.imprint","IMPRINT",FACE,{"disambiguationData":[TD([[makeQuery(id+"F28.imprint","IMPRINT",EDGE,{"derivedFrom":sQuery(id+"F28.wireOp",EDGE,"E84")}),-1.0]])]});
            var Q1;
            {var subQ0=sQuery(id+"F28.wireOp",EDGE,"E181.left");Q1=makeQuery(id+"F44.boolean.opBoolean","MERGE",FACE,{"derivedFrom":[makeQuery(id+"F29.opExtrude","CAP_FACE",FACE,{"disambiguationData":[OSD([sQuery(id+"F28.wireOp",EDGE,"55227c07-3752-4080-a22d-609154aa437d.0"),sQuery(id+"F28.wireOp",EDGE,"55227c07-3752-4080-a22d-609154aa437d.1"),sQuery(id+"F28.wireOp",EDGE,"55227c07-3752-4080-a22d-609154aa437d.2"),sQuery(id+"F28.wireOp",EDGE,"55227c07-3752-4080-a22d-609154aa437d.3"),sQuery(id+"F28.wireOp",EDGE,"E84"),sQuery(id+"F28.wireOp",EDGE,"E86"),sQuery(id+"F28.wireOp",EDGE,"E91.left"),sQuery(id+"F28.wireOp",EDGE,"E91.right"),sQuery(id+"F28.wireOp",EDGE,"E92.left"),sQuery(id+"F28.wireOp",EDGE,"E92.right"),sQuery(id+"F28.wireOp",EDGE,"E93.bottom"),sQuery(id+"F28.wireOp",EDGE,"E93.top"),sQuery(id+"F28.wireOp",EDGE,"E94.trimOffspring"),sQuery(id+"F28.wireOp",EDGE,"E95.trimOffspring"),sQuery(id+"F28.wireOp",EDGE,"E98.trimOffspring"),sQuery(id+"F28.wireOp",EDGE,"E99.trimOffspring"),sQuery(id+"F28.wireOp",EDGE,"E100.trimOffspring"),sQuery(id+"F28.wireOp",EDGE,"E101.trimOffspring"),sQuery(id+"F28.wireOp",EDGE,"E102.trimOffspring"),sQuery(id+"F28.wireOp",EDGE,"E103.trimOffspring"),sQuery(id+"F28.wireOp",EDGE,"E104.bottom"),sQuery(id+"F28.wireOp",EDGE,"E104.left"),sQuery(id+"F28.wireOp",EDGE,"E104.top"),sQuery(id+"F28.wireOp",EDGE,"E104.right"),sQuery(id+"F28.wireOp",EDGE,"E107"),sQuery(id+"F28.wireOp",EDGE,"E109"),sQuery(id+"F28.wireOp",EDGE,"E114.left"),sQuery(id+"F28.wireOp",EDGE,"E114.right"),sQuery(id+"F28.wireOp",EDGE,"E115.left"),sQuery(id+"F28.wireOp",EDGE,"E115.right"),sQuery(id+"F28.wireOp",EDGE,"E116.bottom"),sQuery(id+"F28.wireOp",EDGE,"E116.top"),sQuery(id+"F28.wireOp",EDGE,"E117.trimOffspring"),sQuery(id+"F28.wireOp",EDGE,"E118.trimOffspring"),sQuery(id+"F28.wireOp",EDGE,"E121.trimOffspring"),sQuery(id+"F28.wireOp",EDGE,"E122.trimOffspring"),sQuery(id+"F28.wireOp",EDGE,"E123.trimOffspring"),sQuery(id+"F28.wireOp",EDGE,"E125.trimOffspring"),sQuery(id+"F28.wireOp",EDGE,"E126.trimOffspring"),sQuery(id+"F28.wireOp",EDGE,"E128.trimOffspring"),sQuery(id+"F28.wireOp",EDGE,"E129.bottom"),sQuery(id+"F28.wireOp",EDGE,"E129.left"),sQuery(id+"F28.wireOp",EDGE,"E129.top"),sQuery(id+"F28.wireOp",EDGE,"E129.right"),sQuery(id+"F28.wireOp",EDGE,"E133"),sQuery(id+"F28.wireOp",EDGE,"E135"),sQuery(id+"F28.wireOp",EDGE,"E140.left"),sQuery(id+"F28.wireOp",EDGE,"E140.right"),sQuery(id+"F28.wireOp",EDGE,"E141.left"),sQuery(id+"F28.wireOp",EDGE,"E141.right"),sQuery(id+"F28.wireOp",EDGE,"E142.bottom"),sQuery(id+"F28.wireOp",EDGE,"E142.top"),sQuery(id+"F28.wireOp",EDGE,"E143.trimOffspring"),sQuery(id+"F28.wireOp",EDGE,"E144.trimOffspring"),sQuery(id+"F28.wireOp",EDGE,"E147.trimOffspring"),sQuery(id+"F28.wireOp",EDGE,"E148.trimOffspring"),sQuery(id+"F28.wireOp",EDGE,"E149.trimOffspring"),sQuery(id+"F28.wireOp",EDGE,"E151.trimOffspring"),sQuery(id+"F28.wireOp",EDGE,"E152.trimOffspring"),sQuery(id+"F28.wireOp",EDGE,"E154.trimOffspring"),sQuery(id+"F28.wireOp",EDGE,"E155.bottom"),sQuery(id+"F28.wireOp",EDGE,"E155.left"),sQuery(id+"F28.wireOp",EDGE,"E155.top"),sQuery(id+"F28.wireOp",EDGE,"E155.right"),sQuery(id+"F28.wireOp",EDGE,"E159"),sQuery(id+"F28.wireOp",EDGE,"E161"),sQuery(id+"F28.wireOp",EDGE,"E166.left"),sQuery(id+"F28.wireOp",EDGE,"E166.right"),sQuery(id+"F28.wireOp",EDGE,"E167.left"),sQuery(id+"F28.wireOp",EDGE,"E167.right"),sQuery(id+"F28.wireOp",EDGE,"E168.bottom"),sQuery(id+"F28.wireOp",EDGE,"E168.top"),sQuery(id+"F28.wireOp",EDGE,"E169.trimOffspring"),sQuery(id+"F28.wireOp",EDGE,"E170.trimOffspring"),sQuery(id+"F28.wireOp",EDGE,"E173.trimOffspring"),sQuery(id+"F28.wireOp",EDGE,"E174.trimOffspring"),sQuery(id+"F28.wireOp",EDGE,"E175.trimOffspring"),sQuery(id+"F28.wireOp",EDGE,"E177.trimOffspring"),sQuery(id+"F28.wireOp",EDGE,"E178.trimOffspring"),sQuery(id+"F28.wireOp",EDGE,"E180.trimOffspring"),sQuery(id+"F28.wireOp",EDGE,"E181.bottom"),sQuery(id+"F28.wireOp",EDGE,"E181.top"),subQ0,sQuery(id+"F28.wireOp",EDGE,"E181.right")])],"isStart":true}),makeQuery(id+"F44.opExtrude","SWEPT_FACE",FACE,{"disambiguationData":[OSD([subQ0]),TDD([makeQuery(id+"F29.opExtrude","CAP_EDGE",EDGE,{"disambiguationData":[OSD([subQ0])],"isStart":true})])]})]});}
            extrude(context, id + "F62", {"entities" : qUnion([Q0, Q1]), "operationType" : NewBodyOperationType.ADD, "oppositeDirection" : true, "depth" : 1 * mm});
        }
        {
            var Q0;
            Q0=makeQuery(id+"F31.opExtrude","CAP_FACE",FACE,{"disambiguationData":[OSD([sQuery(id+"F30.wireOp",EDGE,"E182.bottom"),sQuery(id+"F30.wireOp",EDGE,"E182.top"),sQuery(id+"F30.wireOp",EDGE,"E182.left"),sQuery(id+"F30.wireOp",EDGE,"E182.right"),sQuery(id+"F30.wireOp",EDGE,"E183.bottom"),sQuery(id+"F30.wireOp",EDGE,"E183.top"),sQuery(id+"F30.wireOp",EDGE,"E183.left"),sQuery(id+"F30.wireOp",EDGE,"E183.right"),sQuery(id+"F30.wireOp",EDGE,"E186.bottom"),sQuery(id+"F30.wireOp",EDGE,"E186.top"),sQuery(id+"F30.wireOp",EDGE,"E186.left"),sQuery(id+"F30.wireOp",EDGE,"E186.right"),sQuery(id+"F30.wireOp",EDGE,"E189.bottom"),sQuery(id+"F30.wireOp",EDGE,"E189.top"),sQuery(id+"F30.wireOp",EDGE,"E189.left"),sQuery(id+"F30.wireOp",EDGE,"E189.right"),sQuery(id+"F30.wireOp",EDGE,"E192.bottom"),sQuery(id+"F30.wireOp",EDGE,"E192.top"),sQuery(id+"F30.wireOp",EDGE,"E192.left"),sQuery(id+"F30.wireOp",EDGE,"E192.right")])],"isStart":true});
            extrude(context, id + "F63", {"entities" : qUnion([Q0]), "operationType" : NewBodyOperationType.ADD, "depth" : 1 * mm});
        }
        {
            var Q0;
            {var subQ0=sQuery(id+"F36.wireOp",EDGE,"E210.right");var subQ1=sQuery(id+"F36.wireOp",EDGE,"E209.right");var subQ2=sQuery(id+"F34.wireOp",EDGE,"E202.right");Q0=makeQuery(id+"F56.opExtrude","SWEPT_FACE",FACE,{"disambiguationData":[OSD([subQ2,subQ1,subQ0]),TDD([makeQuery(id+"F43.boolean.opBoolean","MERGE",EDGE,{"derivedFrom":[makeQuery(id+"F35.opExtrude","CAP_EDGE",EDGE,{"disambiguationData":[OSD([subQ2])],"isStart":true}),makeQuery(id+"F43.opExtrude","CAP_EDGE",EDGE,{"disambiguationData":[OSD([subQ1])],"isStart":true}),makeQuery(id+"F43.opExtrude","CAP_EDGE",EDGE,{"disambiguationData":[OSD([subQ0])],"isStart":true})]})])]});}
            extrude(context, id + "F64", {"entities" : qUnion([Q0]), "operationType" : NewBodyOperationType.ADD, "depth" : 2 * mm});
        }
        {
            var Q0;
            {var subQ1=sQuery(id+"F9.wireOp",EDGE,"E19.bottom");var subQ2=sQuery(id+"F9.wireOp",EDGE,"E18.right");var subQ3=sQuery(id+"F9.wireOp",EDGE,"E18.top");var subQ4=sQuery(id+"F9.wireOp",EDGE,"E18.bottom");var subQ5=sQuery(id+"F9.wireOp",EDGE,"E17.right");var subQ6=sQuery(id+"F9.wireOp",EDGE,"E17.top");var subQ7=sQuery(id+"F9.wireOp",EDGE,"E17.bottom");var subQ8=sQuery(id+"F9.wireOp",EDGE,"E16.right");var subQ9=sQuery(id+"F9.wireOp",EDGE,"E16.left");var subQ10=sQuery(id+"F9.wireOp",EDGE,"E15.right");var subQ11=sQuery(id+"F9.wireOp",EDGE,"E15.left");var subQ12=sQuery(id+"F9.wireOp",EDGE,"E15.top");var subQ13=makeQuery(id+"F10.opExtrude","CAP_FACE",FACE,{"disambiguationData":[OSD([subQ12,subQ11,subQ10,subQ9,subQ8,subQ7,subQ6,subQ5,subQ4,subQ3,subQ2,subQ1])],"isStart":false});Q0=makeQuery(id+"F42.opFillet","MERGE",FACE,{"derivedFrom":[makeQuery(id+"F10.boolean.opBoolean","SPLIT",FACE,{"disambiguationData":[TD([makeQuery(id+"F10.opExtrude","SWEPT_FACE",FACE,{"disambiguationData":[OSD([subQ12])]})])],"derivedFrom":subQ13}),makeQuery(id+"F10.boolean.opBoolean","SPLIT",FACE,{"disambiguationData":[TD([makeQuery(id+"F10.opExtrude","SWEPT_FACE",FACE,{"disambiguationData":[OSD([subQ1])]})])],"derivedFrom":subQ13}),makeQuery(id+"F10.boolean.opBoolean","SPLIT",FACE,{"disambiguationData":[TD([makeQuery(id+"F10.opExtrude","SWEPT_FACE",FACE,{"disambiguationData":[OSD([subQ5])]})])],"derivedFrom":subQ13}),makeQuery(id+"F10.boolean.opBoolean","SPLIT",FACE,{"disambiguationData":[TD([makeQuery(id+"F10.opExtrude","SWEPT_FACE",FACE,{"disambiguationData":[OSD([subQ2])]})])],"derivedFrom":subQ13})]});}
            extrude(context, id + "F65", {"entities" : qUnion([Q0]), "operationType" : NewBodyOperationType.ADD, "depth" : 0.05 * mm});
        }
        {
            var Q0;
            Q0=makeQuery(id+"F31.opExtrude","CAP_FACE",FACE,{"disambiguationData":[OSD([sQuery(id+"F30.wireOp",EDGE,"E182.bottom"),sQuery(id+"F30.wireOp",EDGE,"E182.top"),sQuery(id+"F30.wireOp",EDGE,"E182.left"),sQuery(id+"F30.wireOp",EDGE,"E182.right"),sQuery(id+"F30.wireOp",EDGE,"E183.bottom"),sQuery(id+"F30.wireOp",EDGE,"E183.top"),sQuery(id+"F30.wireOp",EDGE,"E183.left"),sQuery(id+"F30.wireOp",EDGE,"E183.right"),sQuery(id+"F30.wireOp",EDGE,"E186.bottom"),sQuery(id+"F30.wireOp",EDGE,"E186.top"),sQuery(id+"F30.wireOp",EDGE,"E186.left"),sQuery(id+"F30.wireOp",EDGE,"E186.right"),sQuery(id+"F30.wireOp",EDGE,"E189.bottom"),sQuery(id+"F30.wireOp",EDGE,"E189.top"),sQuery(id+"F30.wireOp",EDGE,"E189.left"),sQuery(id+"F30.wireOp",EDGE,"E189.right"),sQuery(id+"F30.wireOp",EDGE,"E192.bottom"),sQuery(id+"F30.wireOp",EDGE,"E192.top"),sQuery(id+"F30.wireOp",EDGE,"E192.left"),sQuery(id+"F30.wireOp",EDGE,"E192.right")])],"isStart":false});
            var sketch = newSketch(context, id + "F66", { "sketchPlane" : qUnion([Q0])});
            skLineSegment(sketch, "E231.bottom", {"start": v(22.06, -144.26) * mm, "end": v(42.46, -144.26) * mm});
            skLineSegment(sketch, "E231.top", {"start": v(22.06, -141.26) * mm, "end": v(42.46, -141.26) * mm});
            skLineSegment(sketch, "E231.left", {"start": v(22.06, -144.26) * mm, "end": v(22.06, -141.26) * mm});
            skLineSegment(sketch, "E231.right", {"start": v(42.46, -144.26) * mm, "end": v(42.46, -141.26) * mm});
            skLineSegment(sketch, "E232.bottom", {"start": v(22.06, -164.66) * mm, "end": v(42.46, -164.66) * mm});
            skLineSegment(sketch, "E232.top", {"start": v(22.06, -167.66) * mm, "end": v(42.46, -167.66) * mm});
            skLineSegment(sketch, "E232.left", {"start": v(22.06, -164.66) * mm, "end": v(22.06, -167.66) * mm});
            skLineSegment(sketch, "E232.right", {"start": v(42.46, -164.66) * mm, "end": v(42.46, -167.66) * mm});
            skLineSegment(sketch, "E233.bottom", {"start": v(22.06, -141.26) * mm, "end": v(19.06, -141.26) * mm});
            skLineSegment(sketch, "E233.top", {"start": v(22.06, -167.66) * mm, "end": v(19.06, -167.66) * mm});
            skLineSegment(sketch, "E233.left", {"start": v(22.06, -141.26) * mm, "end": v(22.06, -167.66) * mm});
            skLineSegment(sketch, "E233.right", {"start": v(19.06, -141.26) * mm, "end": v(19.06, -167.66) * mm});
            skLineSegment(sketch, "E234.bottom", {"start": v(42.46, -141.26) * mm, "end": v(45.46, -141.26) * mm});
            skLineSegment(sketch, "E234.top", {"start": v(42.46, -167.66) * mm, "end": v(45.46, -167.66) * mm});
            skLineSegment(sketch, "E234.left", {"start": v(42.46, -141.26) * mm, "end": v(42.46, -167.66) * mm});
            skLineSegment(sketch, "E234.right", {"start": v(45.46, -141.26) * mm, "end": v(45.46, -167.66) * mm});
            skLineSegment(sketch, "E235.bottom", {"start": v(52.16, -144.36) * mm, "end": v(72.36, -144.36) * mm});
            skLineSegment(sketch, "E235.top", {"start": v(52.16, -141.26) * mm, "end": v(72.36, -141.26) * mm});
            skLineSegment(sketch, "E235.left", {"start": v(52.16, -144.36) * mm, "end": v(52.16, -141.26) * mm});
            skLineSegment(sketch, "E235.right", {"start": v(72.36, -144.36) * mm, "end": v(72.36, -141.26) * mm});
            skLineSegment(sketch, "E236.bottom", {"start": v(52.16, -141.26) * mm, "end": v(49.16, -141.26) * mm});
            skLineSegment(sketch, "E236.top", {"start": v(52.16, -167.66) * mm, "end": v(49.16, -167.66) * mm});
            skLineSegment(sketch, "E236.left", {"start": v(52.16, -141.26) * mm, "end": v(52.16, -167.66) * mm});
            skLineSegment(sketch, "E236.right", {"start": v(49.16, -141.26) * mm, "end": v(49.16, -167.66) * mm});
            skLineSegment(sketch, "E237.bottom", {"start": v(52.16, -167.66) * mm, "end": v(72.36, -167.66) * mm});
            skLineSegment(sketch, "E237.top", {"start": v(52.16, -164.56) * mm, "end": v(72.36, -164.56) * mm});
            skLineSegment(sketch, "E237.left", {"start": v(52.16, -167.66) * mm, "end": v(52.16, -164.56) * mm});
            skLineSegment(sketch, "E237.right", {"start": v(72.36, -167.66) * mm, "end": v(72.36, -164.56) * mm});
            skLineSegment(sketch, "E238.bottom", {"start": v(72.36, -167.66) * mm, "end": v(75.36, -167.66) * mm});
            skLineSegment(sketch, "E238.top", {"start": v(72.36, -141.26) * mm, "end": v(75.36, -141.26) * mm});
            skLineSegment(sketch, "E238.left", {"start": v(72.36, -167.66) * mm, "end": v(72.36, -141.26) * mm});
            skLineSegment(sketch, "E238.right", {"start": v(75.36, -167.66) * mm, "end": v(75.36, -141.26) * mm});
            skLineSegment(sketch, "E239.bottom", {"start": v(82.16, -144.36) * mm, "end": v(102.36, -144.36) * mm});
            skLineSegment(sketch, "E239.top", {"start": v(82.16, -141.26) * mm, "end": v(102.36, -141.26) * mm});
            skLineSegment(sketch, "E239.left", {"start": v(82.16, -144.36) * mm, "end": v(82.16, -141.26) * mm});
            skLineSegment(sketch, "E239.right", {"start": v(102.36, -144.36) * mm, "end": v(102.36, -141.26) * mm});
            skLineSegment(sketch, "E240.bottom", {"start": v(82.16, -141.26) * mm, "end": v(79.16, -141.26) * mm});
            skLineSegment(sketch, "E240.top", {"start": v(82.16, -167.66) * mm, "end": v(79.16, -167.66) * mm});
            skLineSegment(sketch, "E240.left", {"start": v(82.16, -141.26) * mm, "end": v(82.16, -167.66) * mm});
            skLineSegment(sketch, "E240.right", {"start": v(79.16, -141.26) * mm, "end": v(79.16, -167.66) * mm});
            skLineSegment(sketch, "E241.bottom", {"start": v(82.16, -167.66) * mm, "end": v(102.36, -167.66) * mm});
            skLineSegment(sketch, "E241.top", {"start": v(82.16, -164.56) * mm, "end": v(102.36, -164.56) * mm});
            skLineSegment(sketch, "E241.left", {"start": v(82.16, -167.66) * mm, "end": v(82.16, -164.56) * mm});
            skLineSegment(sketch, "E241.right", {"start": v(102.36, -167.66) * mm, "end": v(102.36, -164.56) * mm});
            skLineSegment(sketch, "E242.bottom", {"start": v(102.36, -141.26) * mm, "end": v(105.36, -141.26) * mm});
            skLineSegment(sketch, "E242.top", {"start": v(102.36, -167.66) * mm, "end": v(105.36, -167.66) * mm});
            skLineSegment(sketch, "E242.left", {"start": v(102.36, -141.26) * mm, "end": v(102.36, -167.66) * mm});
            skLineSegment(sketch, "E242.right", {"start": v(105.36, -141.26) * mm, "end": v(105.36, -167.66) * mm});
            skLineSegment(sketch, "E243.bottom", {"start": v(112.16, -144.36) * mm, "end": v(132.36, -144.36) * mm});
            skLineSegment(sketch, "E243.top", {"start": v(112.16, -141.26) * mm, "end": v(132.36, -141.26) * mm});
            skLineSegment(sketch, "E243.left", {"start": v(112.16, -144.36) * mm, "end": v(112.16, -141.26) * mm});
            skLineSegment(sketch, "E243.right", {"start": v(132.36, -144.36) * mm, "end": v(132.36, -141.26) * mm});
            skLineSegment(sketch, "E244.bottom", {"start": v(112.16, -141.26) * mm, "end": v(109.16, -141.26) * mm});
            skLineSegment(sketch, "E244.top", {"start": v(112.16, -167.66) * mm, "end": v(109.16, -167.66) * mm});
            skLineSegment(sketch, "E244.left", {"start": v(112.16, -141.26) * mm, "end": v(112.16, -167.66) * mm});
            skLineSegment(sketch, "E244.right", {"start": v(109.16, -141.26) * mm, "end": v(109.16, -167.66) * mm});
            skLineSegment(sketch, "E245.bottom", {"start": v(112.16, -167.66) * mm, "end": v(132.36, -167.66) * mm});
            skLineSegment(sketch, "E245.top", {"start": v(112.16, -164.56) * mm, "end": v(132.36, -164.56) * mm});
            skLineSegment(sketch, "E245.left", {"start": v(112.16, -167.66) * mm, "end": v(112.16, -164.56) * mm});
            skLineSegment(sketch, "E245.right", {"start": v(132.36, -167.66) * mm, "end": v(132.36, -164.56) * mm});
            skLineSegment(sketch, "E246.bottom", {"start": v(132.36, -141.26) * mm, "end": v(135.36, -141.26) * mm});
            skLineSegment(sketch, "E246.top", {"start": v(132.36, -167.66) * mm, "end": v(135.36, -167.66) * mm});
            skLineSegment(sketch, "E246.left", {"start": v(132.36, -141.26) * mm, "end": v(132.36, -167.66) * mm});
            skLineSegment(sketch, "E246.right", {"start": v(135.36, -141.26) * mm, "end": v(135.36, -167.66) * mm});
            skSolve(sketch);
        }
        {
            var Q0;
            Q0=qSketchRegion(id+"F66",true);
            extrude(context, id + "F67", {"entities" : qUnion([Q0]), "operationType" : NewBodyOperationType.ADD, "depth" : 0.5 * mm});
        }
        {
            var Q0;
            Q0=makeQuery(id+"F67.opExtrude","CAP_FACE",FACE,{"disambiguationData":[OSD([sQuery(id+"F66.wireOp",EDGE,"E231.bottom"),sQuery(id+"F66.wireOp",EDGE,"E231.top"),sQuery(id+"F66.wireOp",EDGE,"E232.bottom"),sQuery(id+"F66.wireOp",EDGE,"E232.top"),sQuery(id+"F66.wireOp",EDGE,"E233.bottom"),sQuery(id+"F66.wireOp",EDGE,"E233.top"),sQuery(id+"F66.wireOp",EDGE,"E233.left"),sQuery(id+"F66.wireOp",EDGE,"E233.right"),sQuery(id+"F66.wireOp",EDGE,"E234.bottom"),sQuery(id+"F66.wireOp",EDGE,"E234.top"),sQuery(id+"F66.wireOp",EDGE,"E234.left"),sQuery(id+"F66.wireOp",EDGE,"E234.right")])],"isStart":false});
            var sketch = newSketch(context, id + "F68", { "sketchPlane" : qUnion([Q0])});
            skLineSegment(sketch, "E247.bottom", {"start": v(22.06, -144.26) * mm, "end": v(42.46, -144.26) * mm});
            skLineSegment(sketch, "E247.top", {"start": v(22.06, -142.76) * mm, "end": v(42.46, -142.76) * mm});
            skLineSegment(sketch, "E247.left", {"start": v(22.06, -144.26) * mm, "end": v(22.06, -142.76) * mm});
            skLineSegment(sketch, "E247.right", {"start": v(42.46, -144.26) * mm, "end": v(42.46, -142.76) * mm});
            skLineSegment(sketch, "E248.bottom", {"start": v(22.06, -164.66) * mm, "end": v(42.46, -164.66) * mm});
            skLineSegment(sketch, "E248.top", {"start": v(22.06, -166.16) * mm, "end": v(42.46, -166.16) * mm});
            skLineSegment(sketch, "E248.left", {"start": v(22.06, -164.66) * mm, "end": v(22.06, -166.16) * mm});
            skLineSegment(sketch, "E248.right", {"start": v(42.46, -164.66) * mm, "end": v(42.46, -166.16) * mm});
            skLineSegment(sketch, "E249.bottom", {"start": v(22.06, -166.16) * mm, "end": v(20.56, -166.16) * mm});
            skLineSegment(sketch, "E249.top", {"start": v(22.06, -142.76) * mm, "end": v(20.56, -142.76) * mm});
            skLineSegment(sketch, "E249.left", {"start": v(22.06, -166.16) * mm, "end": v(22.06, -142.76) * mm});
            skLineSegment(sketch, "E249.right", {"start": v(20.56, -166.16) * mm, "end": v(20.56, -142.76) * mm});
            skLineSegment(sketch, "E250.bottom", {"start": v(42.46, -166.16) * mm, "end": v(43.96, -166.16) * mm});
            skLineSegment(sketch, "E250.top", {"start": v(42.46, -142.76) * mm, "end": v(43.96, -142.76) * mm});
            skLineSegment(sketch, "E250.left", {"start": v(42.46, -166.16) * mm, "end": v(42.46, -142.76) * mm});
            skLineSegment(sketch, "E250.right", {"start": v(43.96, -166.16) * mm, "end": v(43.96, -142.76) * mm});
            skLineSegment(sketch, "E251.bottom", {"start": v(50.66, -142.86) * mm, "end": v(52.16, -142.86) * mm});
            skLineSegment(sketch, "E251.top", {"start": v(50.66, -166.06) * mm, "end": v(52.16, -166.06) * mm});
            skLineSegment(sketch, "E251.left", {"start": v(50.66, -142.86) * mm, "end": v(50.66, -166.06) * mm});
            skLineSegment(sketch, "E251.right", {"start": v(52.16, -142.86) * mm, "end": v(52.16, -166.06) * mm});
            skLineSegment(sketch, "E252.bottom", {"start": v(72.36, -142.86) * mm, "end": v(73.86, -142.86) * mm});
            skLineSegment(sketch, "E252.top", {"start": v(72.36, -166.06) * mm, "end": v(73.86, -166.06) * mm});
            skLineSegment(sketch, "E252.left", {"start": v(72.36, -142.86) * mm, "end": v(72.36, -166.06) * mm});
            skLineSegment(sketch, "E252.right", {"start": v(73.86, -142.86) * mm, "end": v(73.86, -166.06) * mm});
            skLineSegment(sketch, "E253.bottom", {"start": v(52.16, -142.86) * mm, "end": v(72.36, -142.86) * mm});
            skLineSegment(sketch, "E253.top", {"start": v(52.16, -144.36) * mm, "end": v(72.36, -144.36) * mm});
            skLineSegment(sketch, "E253.left", {"start": v(52.16, -142.86) * mm, "end": v(52.16, -144.36) * mm});
            skLineSegment(sketch, "E253.right", {"start": v(72.36, -142.86) * mm, "end": v(72.36, -144.36) * mm});
            skLineSegment(sketch, "E254.bottom", {"start": v(52.16, -166.06) * mm, "end": v(72.36, -166.06) * mm});
            skLineSegment(sketch, "E254.top", {"start": v(52.16, -164.56) * mm, "end": v(72.36, -164.56) * mm});
            skLineSegment(sketch, "E254.left", {"start": v(52.16, -166.06) * mm, "end": v(52.16, -164.56) * mm});
            skLineSegment(sketch, "E254.right", {"start": v(72.36, -166.06) * mm, "end": v(72.36, -164.56) * mm});
            skLineSegment(sketch, "E255.bottom", {"start": v(80.66, -142.86) * mm, "end": v(82.16, -142.86) * mm});
            skLineSegment(sketch, "E255.top", {"start": v(80.66, -166.06) * mm, "end": v(82.16, -166.06) * mm});
            skLineSegment(sketch, "E255.left", {"start": v(80.66, -142.86) * mm, "end": v(80.66, -166.06) * mm});
            skLineSegment(sketch, "E255.right", {"start": v(82.16, -142.86) * mm, "end": v(82.16, -166.06) * mm});
            skLineSegment(sketch, "E256.bottom", {"start": v(82.16, -142.86) * mm, "end": v(102.36, -142.86) * mm});
            skLineSegment(sketch, "E256.top", {"start": v(82.16, -144.36) * mm, "end": v(102.36, -144.36) * mm});
            skLineSegment(sketch, "E256.left", {"start": v(82.16, -142.86) * mm, "end": v(82.16, -144.36) * mm});
            skLineSegment(sketch, "E256.right", {"start": v(102.36, -142.86) * mm, "end": v(102.36, -144.36) * mm});
            skLineSegment(sketch, "E257.bottom", {"start": v(82.16, -166.06) * mm, "end": v(102.36, -166.06) * mm});
            skLineSegment(sketch, "E257.top", {"start": v(82.16, -164.56) * mm, "end": v(102.36, -164.56) * mm});
            skLineSegment(sketch, "E257.left", {"start": v(82.16, -166.06) * mm, "end": v(82.16, -164.56) * mm});
            skLineSegment(sketch, "E257.right", {"start": v(102.36, -166.06) * mm, "end": v(102.36, -164.56) * mm});
            skLineSegment(sketch, "E258.bottom", {"start": v(102.36, -166.06) * mm, "end": v(103.86, -166.06) * mm});
            skLineSegment(sketch, "E258.top", {"start": v(102.36, -142.86) * mm, "end": v(103.86, -142.86) * mm});
            skLineSegment(sketch, "E258.left", {"start": v(102.36, -166.06) * mm, "end": v(102.36, -142.86) * mm});
            skLineSegment(sketch, "E258.right", {"start": v(103.86, -166.06) * mm, "end": v(103.86, -142.86) * mm});
            skLineSegment(sketch, "E259.bottom", {"start": v(110.76, -142.86) * mm, "end": v(112.26, -142.86) * mm});
            skLineSegment(sketch, "E259.top", {"start": v(110.76, -166.06) * mm, "end": v(112.26, -166.06) * mm});
            skLineSegment(sketch, "E259.left", {"start": v(110.76, -142.86) * mm, "end": v(110.76, -166.06) * mm});
            skLineSegment(sketch, "E259.right", {"start": v(112.26, -142.86) * mm, "end": v(112.26, -166.06) * mm});
            skLineSegment(sketch, "E260.bottom", {"start": v(112.26, -142.86) * mm, "end": v(132.46, -142.86) * mm});
            skLineSegment(sketch, "E260.top", {"start": v(112.26, -144.36) * mm, "end": v(132.46, -144.36) * mm});
            skLineSegment(sketch, "E260.left", {"start": v(112.26, -142.86) * mm, "end": v(112.26, -144.36) * mm});
            skLineSegment(sketch, "E260.right", {"start": v(132.46, -142.86) * mm, "end": v(132.46, -144.36) * mm});
            skLineSegment(sketch, "E261.bottom", {"start": v(112.26, -166.06) * mm, "end": v(132.46, -166.06) * mm});
            skLineSegment(sketch, "E261.top", {"start": v(112.26, -164.56) * mm, "end": v(132.46, -164.56) * mm});
            skLineSegment(sketch, "E261.left", {"start": v(112.26, -166.06) * mm, "end": v(112.26, -164.56) * mm});
            skLineSegment(sketch, "E261.right", {"start": v(132.46, -166.06) * mm, "end": v(132.46, -164.56) * mm});
            skLineSegment(sketch, "E262.bottom", {"start": v(132.46, -166.06) * mm, "end": v(133.96, -166.06) * mm});
            skLineSegment(sketch, "E262.top", {"start": v(132.46, -142.86) * mm, "end": v(133.96, -142.86) * mm});
            skLineSegment(sketch, "E262.left", {"start": v(132.46, -166.06) * mm, "end": v(132.46, -142.86) * mm});
            skLineSegment(sketch, "E262.right", {"start": v(133.96, -166.06) * mm, "end": v(133.96, -142.86) * mm});
            skSolve(sketch);
        }
        {
            var Q0;
            Q0=qSketchRegion(id+"F68",true);
            extrude(context, id + "F69", {"entities" : qUnion([Q0]), "operationType" : NewBodyOperationType.ADD, "depth" : 1 * mm});
        }
        {
            var Q0;
            Q0=makeQuery(id+"F67.opExtrude","SWEPT_EDGE",EDGE,{"disambiguationData":[OSD([sQuery(id+"F66.wireOp",EDGE,"E233.bottom"),sQuery(id+"F66.wireOp",EDGE,"E233.right")])]});
            var Q1;
            Q1=makeQuery(id+"F69.opExtrude","SWEPT_EDGE",EDGE,{"disambiguationData":[OSD([sQuery(id+"F68.wireOp",EDGE,"E249.top"),sQuery(id+"F68.wireOp",EDGE,"E249.right")])]});
            var Q2;
            Q2=makeQuery(id+"F67.opExtrude","SWEPT_EDGE",EDGE,{"disambiguationData":[OSD([sQuery(id+"F66.wireOp",EDGE,"E233.top"),sQuery(id+"F66.wireOp",EDGE,"E233.right")])]});
            var Q3;
            Q3=makeQuery(id+"F69.opExtrude","SWEPT_EDGE",EDGE,{"disambiguationData":[OSD([sQuery(id+"F68.wireOp",EDGE,"E249.bottom"),sQuery(id+"F68.wireOp",EDGE,"E249.right")])]});
            var Q4;
            Q4=makeQuery(id+"F69.opExtrude","SWEPT_EDGE",EDGE,{"disambiguationData":[OSD([sQuery(id+"F68.wireOp",EDGE,"E250.bottom"),sQuery(id+"F68.wireOp",EDGE,"E250.right")])]});
            var Q5;
            Q5=makeQuery(id+"F67.opExtrude","SWEPT_EDGE",EDGE,{"disambiguationData":[OSD([sQuery(id+"F66.wireOp",EDGE,"E234.top"),sQuery(id+"F66.wireOp",EDGE,"E234.right")])]});
            var Q6;
            Q6=makeQuery(id+"F69.opExtrude","SWEPT_EDGE",EDGE,{"disambiguationData":[OSD([sQuery(id+"F68.wireOp",EDGE,"E250.top"),sQuery(id+"F68.wireOp",EDGE,"E250.right")])]});
            var Q7;
            Q7=makeQuery(id+"F67.opExtrude","SWEPT_EDGE",EDGE,{"disambiguationData":[OSD([sQuery(id+"F66.wireOp",EDGE,"E234.bottom"),sQuery(id+"F66.wireOp",EDGE,"E234.right")])]});
            var Q8;
            Q8=makeQuery(id+"F67.opExtrude","SWEPT_EDGE",EDGE,{"disambiguationData":[OSD([sQuery(id+"F66.wireOp",EDGE,"E236.bottom"),sQuery(id+"F66.wireOp",EDGE,"E236.right")])]});
            var Q9;
            Q9=makeQuery(id+"F69.opExtrude","SWEPT_EDGE",EDGE,{"disambiguationData":[OSD([sQuery(id+"F68.wireOp",EDGE,"E251.bottom"),sQuery(id+"F68.wireOp",EDGE,"E251.left")])]});
            var Q10;
            Q10=makeQuery(id+"F69.opExtrude","SWEPT_EDGE",EDGE,{"disambiguationData":[OSD([sQuery(id+"F68.wireOp",EDGE,"E251.top"),sQuery(id+"F68.wireOp",EDGE,"E251.left")])]});
            var Q11;
            Q11=makeQuery(id+"F67.opExtrude","SWEPT_EDGE",EDGE,{"disambiguationData":[OSD([sQuery(id+"F66.wireOp",EDGE,"E236.top"),sQuery(id+"F66.wireOp",EDGE,"E236.right")])]});
            var Q12;
            Q12=makeQuery(id+"F69.opExtrude","SWEPT_EDGE",EDGE,{"disambiguationData":[OSD([sQuery(id+"F68.wireOp",EDGE,"E252.top"),sQuery(id+"F68.wireOp",EDGE,"E252.right")])]});
            var Q13;
            Q13=makeQuery(id+"F67.opExtrude","SWEPT_EDGE",EDGE,{"disambiguationData":[OSD([sQuery(id+"F66.wireOp",EDGE,"E238.bottom"),sQuery(id+"F66.wireOp",EDGE,"E238.right")])]});
            var Q14;
            Q14=makeQuery(id+"F69.opExtrude","SWEPT_EDGE",EDGE,{"disambiguationData":[OSD([sQuery(id+"F68.wireOp",EDGE,"E252.bottom"),sQuery(id+"F68.wireOp",EDGE,"E252.right")])]});
            var Q15;
            Q15=makeQuery(id+"F67.opExtrude","SWEPT_EDGE",EDGE,{"disambiguationData":[OSD([sQuery(id+"F66.wireOp",EDGE,"E238.top"),sQuery(id+"F66.wireOp",EDGE,"E238.right")])]});
            var Q16;
            Q16=makeQuery(id+"F67.opExtrude","SWEPT_EDGE",EDGE,{"disambiguationData":[OSD([sQuery(id+"F66.wireOp",EDGE,"E240.bottom"),sQuery(id+"F66.wireOp",EDGE,"E240.right")])]});
            var Q17;
            Q17=makeQuery(id+"F69.opExtrude","SWEPT_EDGE",EDGE,{"disambiguationData":[OSD([sQuery(id+"F68.wireOp",EDGE,"E255.bottom"),sQuery(id+"F68.wireOp",EDGE,"E255.left")])]});
            var Q18;
            Q18=makeQuery(id+"F67.opExtrude","SWEPT_EDGE",EDGE,{"disambiguationData":[OSD([sQuery(id+"F66.wireOp",EDGE,"E240.top"),sQuery(id+"F66.wireOp",EDGE,"E240.right")])]});
            var Q19;
            Q19=makeQuery(id+"F69.opExtrude","SWEPT_EDGE",EDGE,{"disambiguationData":[OSD([sQuery(id+"F68.wireOp",EDGE,"E255.top"),sQuery(id+"F68.wireOp",EDGE,"E255.left")])]});
            var Q20;
            Q20=makeQuery(id+"F69.opExtrude","SWEPT_EDGE",EDGE,{"disambiguationData":[OSD([sQuery(id+"F68.wireOp",EDGE,"E258.bottom"),sQuery(id+"F68.wireOp",EDGE,"E258.right")])]});
            var Q21;
            Q21=makeQuery(id+"F67.opExtrude","SWEPT_EDGE",EDGE,{"disambiguationData":[OSD([sQuery(id+"F66.wireOp",EDGE,"E242.top"),sQuery(id+"F66.wireOp",EDGE,"E242.right")])]});
            var Q22;
            Q22=makeQuery(id+"F69.opExtrude","SWEPT_EDGE",EDGE,{"disambiguationData":[OSD([sQuery(id+"F68.wireOp",EDGE,"E258.top"),sQuery(id+"F68.wireOp",EDGE,"E258.right")])]});
            var Q23;
            Q23=makeQuery(id+"F67.opExtrude","SWEPT_EDGE",EDGE,{"disambiguationData":[OSD([sQuery(id+"F66.wireOp",EDGE,"E242.bottom"),sQuery(id+"F66.wireOp",EDGE,"E242.right")])]});
            var Q24;
            Q24=makeQuery(id+"F67.opExtrude","SWEPT_EDGE",EDGE,{"disambiguationData":[OSD([sQuery(id+"F66.wireOp",EDGE,"E244.bottom"),sQuery(id+"F66.wireOp",EDGE,"E244.right")])]});
            var Q25;
            Q25=makeQuery(id+"F69.opExtrude","SWEPT_EDGE",EDGE,{"disambiguationData":[OSD([sQuery(id+"F68.wireOp",EDGE,"E259.bottom"),sQuery(id+"F68.wireOp",EDGE,"E259.left")])]});
            var Q26;
            Q26=makeQuery(id+"F67.opExtrude","SWEPT_EDGE",EDGE,{"disambiguationData":[OSD([sQuery(id+"F66.wireOp",EDGE,"E244.top"),sQuery(id+"F66.wireOp",EDGE,"E244.right")])]});
            var Q27;
            Q27=makeQuery(id+"F69.opExtrude","SWEPT_EDGE",EDGE,{"disambiguationData":[OSD([sQuery(id+"F68.wireOp",EDGE,"E259.top"),sQuery(id+"F68.wireOp",EDGE,"E259.left")])]});
            var Q28;
            Q28=makeQuery(id+"F69.opExtrude","SWEPT_EDGE",EDGE,{"disambiguationData":[OSD([sQuery(id+"F68.wireOp",EDGE,"E262.bottom"),sQuery(id+"F68.wireOp",EDGE,"E262.right")])]});
            var Q29;
            Q29=makeQuery(id+"F67.opExtrude","SWEPT_EDGE",EDGE,{"disambiguationData":[OSD([sQuery(id+"F66.wireOp",EDGE,"E246.top"),sQuery(id+"F66.wireOp",EDGE,"E246.right")])]});
            var Q30;
            Q30=makeQuery(id+"F69.opExtrude","SWEPT_EDGE",EDGE,{"disambiguationData":[OSD([sQuery(id+"F68.wireOp",EDGE,"E262.top"),sQuery(id+"F68.wireOp",EDGE,"E262.right")])]});
            var Q31;
            Q31=makeQuery(id+"F67.opExtrude","SWEPT_EDGE",EDGE,{"disambiguationData":[OSD([sQuery(id+"F66.wireOp",EDGE,"E246.bottom"),sQuery(id+"F66.wireOp",EDGE,"E246.right")])]});
            fillet(context, id + "F70", {"entities" : qUnion([Q0, Q1, Q2, Q3, Q4, Q5, Q6, Q7, Q8, Q9, Q10, Q11, Q12, Q13, Q14, Q15, Q16, Q17, Q18, Q19, Q20, Q21, Q22, Q23, Q24, Q25, Q26, Q27, Q28, Q29, Q30, Q31]), "radius" : 0.5 * mm, "tangentPropagation" : true, "allowEdgeOverflow" : false});
        }
        {
            var Q0;
            Q0=makeQuery(id+"F8.opExtrude","CAP_FACE",FACE,{"disambiguationData":[OSD([sQuery(id+"F7.wireOp",EDGE,"E14.bottom"),sQuery(id+"F7.wireOp",EDGE,"E14.top"),sQuery(id+"F7.wireOp",EDGE,"E14.left"),sQuery(id+"F7.wireOp",EDGE,"E14.right")])],"isStart":false});
            var sketch = newSketch(context, id + "F71", { "sketchPlane" : qUnion([Q0])});
            skLineSegment(sketch, "E263.bottom", {"start": v(-87.88, 7.7) * mm, "end": v(-69.88, 7.7) * mm});
            skLineSegment(sketch, "E263.top", {"start": v(-87.88, -10.3) * mm, "end": v(-69.88, -10.3) * mm});
            skLineSegment(sketch, "E263.left", {"start": v(-87.88, 7.7) * mm, "end": v(-87.88, -10.3) * mm});
            skLineSegment(sketch, "E263.right", {"start": v(-69.88, 7.7) * mm, "end": v(-69.88, -10.3) * mm});
            skSolve(sketch);
        }
        {
            var Q0;
            Q0=qSketchRegion(id+"F71",true);
            extrude(context, id + "F72", {"entities" : qUnion([Q0]), "operationType" : NewBodyOperationType.REMOVE, "oppositeDirection" : true, "depth" : 1 * mm});
        }
        {
            var Q0;
            Q0=qCreatedBy(makeId("Top.planeOp"),FACE);
            var sketch = newSketch(context, id + "F73", { "sketchPlane" : qUnion([Q0])});
            skLineSegment(sketch, "E264.bottom", {"start": v(-55.36, 28.1) * mm, "end": v(-37.56, 28.1) * mm});
            skLineSegment(sketch, "E264.top", {"start": v(-55.36, 10.3) * mm, "end": v(-37.56, 10.3) * mm});
            skLineSegment(sketch, "E264.left", {"start": v(-55.36, 28.1) * mm, "end": v(-55.36, 10.3) * mm});
            skLineSegment(sketch, "E264.right", {"start": v(-37.56, 28.1) * mm, "end": v(-37.56, 10.3) * mm});
            skSolve(sketch);
        }
        {
            var Q0;
            Q0=qSketchRegion(id+"F73",true);
            extrude(context, id + "F74", {"entities" : qUnion([Q0]), "depth" : 1 * mm});
        }
        {
            var Q0;
            Q0=makeQuery(id+"F1.opExtrude","CAP_FACE",FACE,{"disambiguationData":[OSD([sQuery(id+"F0.wireOp",EDGE,"E1.bottom"),sQuery(id+"F0.wireOp",EDGE,"E1.top"),sQuery(id+"F0.wireOp",EDGE,"E1.left"),sQuery(id+"F0.wireOp",EDGE,"E1.right")])],"isStart":false});
            var sketch = newSketch(context, id + "F75", { "sketchPlane" : qUnion([Q0])});
            skLineSegment(sketch, "E265.bottom", {"start": v(9, 9) * mm, "end": v(-9, 9) * mm});
            skLineSegment(sketch, "E265.top", {"start": v(9, -9) * mm, "end": v(-9, -9) * mm});
            skLineSegment(sketch, "E265.left", {"start": v(9, 9) * mm, "end": v(9, -9) * mm});
            skLineSegment(sketch, "E265.right", {"start": v(-9, 9) * mm, "end": v(-9, -9) * mm});
            skPoint(sketch, "E265.middle", {"position": v(0, 0) * mm});
            skSolve(sketch);
        }
        {
            var Q0;
            Q0=qSketchRegion(id+"F75",true);
            extrude(context, id + "F76", {"entities" : qUnion([Q0]), "operationType" : NewBodyOperationType.REMOVE, "oppositeDirection" : true, "depth" : 1 * mm});
        }
    });
